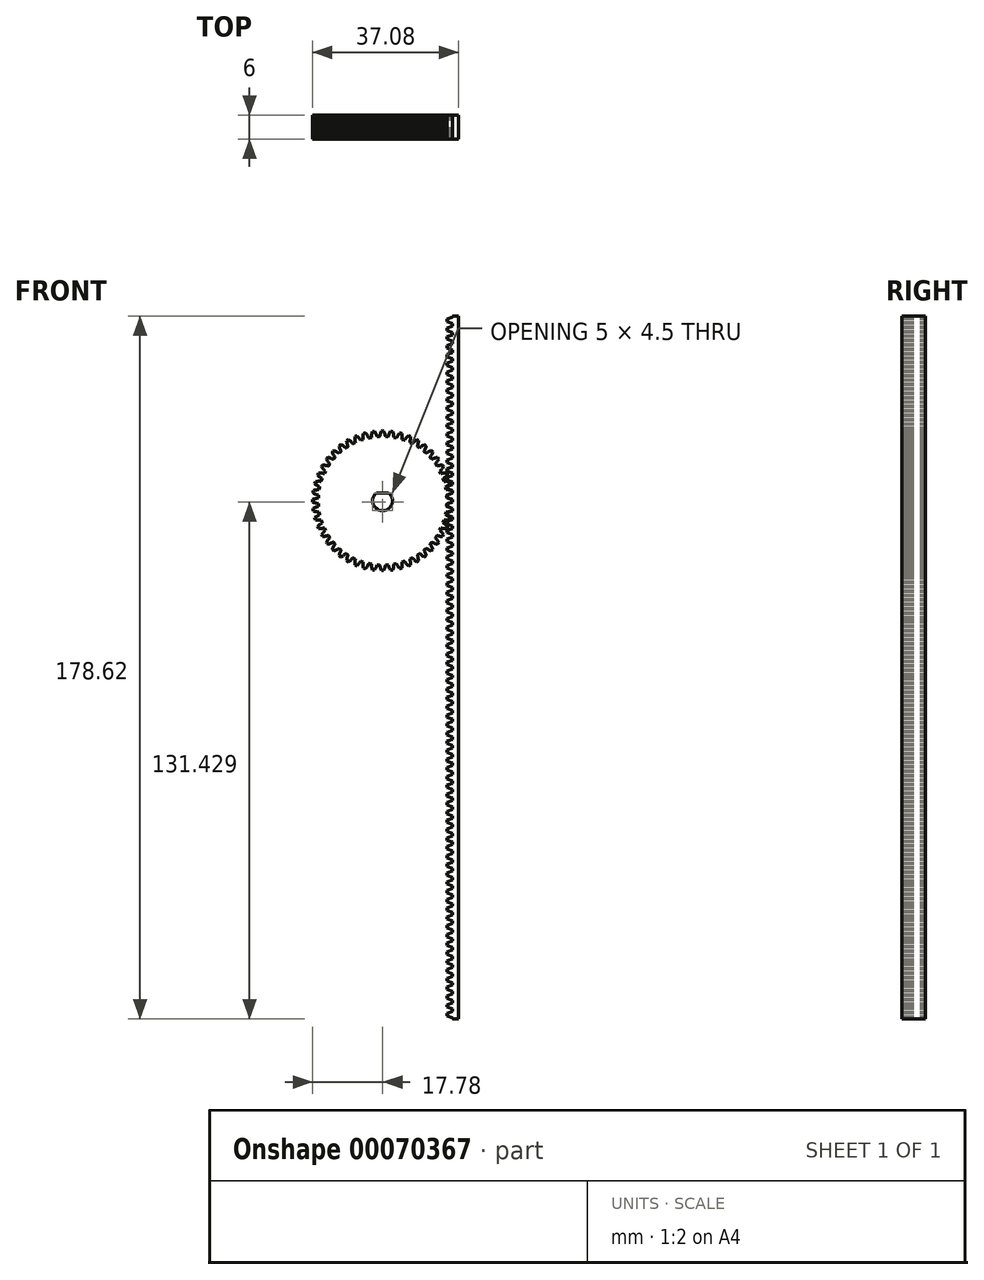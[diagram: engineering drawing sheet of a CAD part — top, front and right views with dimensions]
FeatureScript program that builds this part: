
annotation { "Feature Type Name" : "Feature", "Feature Type Description" : "" }
export const myFeature = defineFeature(function(context is Context, id is Id, definition is map)
    precondition{}
    {
        {
            var Q0;
            Q0=qCreatedBy(makeId("Front.planeOp"),FACE);
            var sketch = newSketch(context, id + "F0", { "sketchPlane" : qUnion([Q0])});
            skLineSegment(sketch, "E0", {"start": v(16.14, -3.72) * mm, "end": v(16.2, -3.44) * mm});
            skLineSegment(sketch, "E1", {"start": v(16.2, -3.44) * mm, "end": v(16.22, -3.15) * mm});
            skLineSegment(sketch, "E2", {"start": v(16.22, -3.15) * mm, "end": v(15.98, -3) * mm});
            skLineSegment(sketch, "E3", {"start": v(15.98, -3) * mm, "end": v(15.73, -2.88) * mm});
            skLineSegment(sketch, "E4", {"start": v(15.73, -2.88) * mm, "end": v(15.5, -2.77) * mm});
            skLineSegment(sketch, "E5", {"start": v(15.5, -2.77) * mm, "end": v(15.3, -2.69) * mm});
            skLineSegment(sketch, "E6", {"start": v(15.3, -2.69) * mm, "end": v(15.13, -2.62) * mm});
            skLineSegment(sketch, "E7", {"start": v(15.13, -2.62) * mm, "end": v(14.95, -2.57) * mm});
            skLineSegment(sketch, "E8", {"start": v(14.95, -2.57) * mm, "end": v(14.89, -2.54) * mm});
            skLineSegment(sketch, "E9", {"start": v(14.89, -2.54) * mm, "end": v(14.86, -2.5) * mm});
            skLineSegment(sketch, "E10", {"start": v(14.86, -2.5) * mm, "end": v(14.9, -1.87) * mm});
            skLineSegment(sketch, "E11", {"start": v(14.9, -1.87) * mm, "end": v(14.93, -1.84) * mm});
            skLineSegment(sketch, "E12", {"start": v(14.93, -1.84) * mm, "end": v(15, -1.82) * mm});
            skLineSegment(sketch, "E13", {"start": v(15, -1.82) * mm, "end": v(15.18, -1.78) * mm});
            skLineSegment(sketch, "E14", {"start": v(15.18, -1.78) * mm, "end": v(15.36, -1.74) * mm});
            skLineSegment(sketch, "E15", {"start": v(15.36, -1.74) * mm, "end": v(15.57, -1.69) * mm});
            skLineSegment(sketch, "E16", {"start": v(15.57, -1.69) * mm, "end": v(15.81, -1.61) * mm});
            skLineSegment(sketch, "E17", {"start": v(15.81, -1.61) * mm, "end": v(16.07, -1.52) * mm});
            skLineSegment(sketch, "E18", {"start": v(16.07, -1.52) * mm, "end": v(16.33, -1.4) * mm});
            skLineSegment(sketch, "E19", {"start": v(16.33, -1.4) * mm, "end": v(16.35, -1.12) * mm});
            skLineSegment(sketch, "E20", {"start": v(16.35, -1.12) * mm, "end": v(16.33, -0.83) * mm});
            skLineSegment(sketch, "E21", {"start": v(16.33, -0.83) * mm, "end": v(16.07, -0.72) * mm});
            skLineSegment(sketch, "E22", {"start": v(16.07, -0.72) * mm, "end": v(15.81, -0.62) * mm});
            skLineSegment(sketch, "E23", {"start": v(15.81, -0.62) * mm, "end": v(15.57, -0.55) * mm});
            skLineSegment(sketch, "E24", {"start": v(15.57, -0.55) * mm, "end": v(15.36, -0.5) * mm});
            skLineSegment(sketch, "E25", {"start": v(15.36, -0.5) * mm, "end": v(15.18, -0.45) * mm});
            skLineSegment(sketch, "E26", {"start": v(15.18, -0.45) * mm, "end": v(15, -0.42) * mm});
            skLineSegment(sketch, "E27", {"start": v(15, -0.42) * mm, "end": v(14.93, -0.4) * mm});
            skLineSegment(sketch, "E28", {"start": v(14.93, -0.4) * mm, "end": v(14.9, -0.37) * mm});
            skLineSegment(sketch, "E29", {"start": v(14.9, -0.37) * mm, "end": v(14.86, 0.27) * mm});
            skLineSegment(sketch, "E30", {"start": v(14.86, 0.27) * mm, "end": v(14.89, 0.3) * mm});
            skLineSegment(sketch, "E31", {"start": v(14.89, 0.3) * mm, "end": v(14.95, 0.33) * mm});
            skLineSegment(sketch, "E32", {"start": v(14.95, 0.33) * mm, "end": v(15.13, 0.39) * mm});
            skLineSegment(sketch, "E33", {"start": v(15.13, 0.39) * mm, "end": v(15.3, 0.45) * mm});
            skLineSegment(sketch, "E34", {"start": v(15.3, 0.45) * mm, "end": v(15.5, 0.54) * mm});
            skLineSegment(sketch, "E35", {"start": v(15.5, 0.54) * mm, "end": v(15.73, 0.64) * mm});
            skLineSegment(sketch, "E36", {"start": v(15.73, 0.64) * mm, "end": v(15.98, 0.77) * mm});
            skLineSegment(sketch, "E37", {"start": v(15.98, 0.77) * mm, "end": v(16.22, 0.91) * mm});
            skLineSegment(sketch, "E38", {"start": v(16.22, 0.91) * mm, "end": v(16.2, 1.2) * mm});
            skLineSegment(sketch, "E39", {"start": v(16.2, 1.2) * mm, "end": v(16.14, 1.49) * mm});
            skLineSegment(sketch, "E40", {"start": v(16.14, 1.49) * mm, "end": v(15.87, 1.56) * mm});
            skLineSegment(sketch, "E41", {"start": v(15.87, 1.56) * mm, "end": v(15.6, 1.62) * mm});
            skLineSegment(sketch, "E42", {"start": v(15.6, 1.62) * mm, "end": v(15.35, 1.67) * mm});
            skLineSegment(sketch, "E43", {"start": v(15.35, 1.67) * mm, "end": v(15.14, 1.7) * mm});
            skLineSegment(sketch, "E44", {"start": v(15.14, 1.7) * mm, "end": v(14.95, 1.71) * mm});
            skLineSegment(sketch, "E45", {"start": v(14.95, 1.71) * mm, "end": v(14.77, 1.72) * mm});
            skLineSegment(sketch, "E46", {"start": v(14.77, 1.72) * mm, "end": v(14.7, 1.74) * mm});
            skLineSegment(sketch, "E47", {"start": v(14.7, 1.74) * mm, "end": v(14.66, 1.76) * mm});
            skLineSegment(sketch, "E48", {"start": v(14.66, 1.76) * mm, "end": v(14.54, 2.38) * mm});
            skLineSegment(sketch, "E49", {"start": v(14.54, 2.38) * mm, "end": v(14.56, 2.42) * mm});
            skLineSegment(sketch, "E50", {"start": v(14.56, 2.42) * mm, "end": v(14.62, 2.46) * mm});
            skLineSegment(sketch, "E51", {"start": v(14.62, 2.46) * mm, "end": v(14.79, 2.54) * mm});
            skLineSegment(sketch, "E52", {"start": v(14.79, 2.54) * mm, "end": v(14.95, 2.62) * mm});
            skLineSegment(sketch, "E53", {"start": v(14.95, 2.62) * mm, "end": v(15.14, 2.73) * mm});
            skLineSegment(sketch, "E54", {"start": v(15.14, 2.73) * mm, "end": v(15.35, 2.87) * mm});
            skLineSegment(sketch, "E55", {"start": v(15.35, 2.87) * mm, "end": v(15.58, 3.03) * mm});
            skLineSegment(sketch, "E56", {"start": v(15.58, 3.03) * mm, "end": v(15.8, 3.2) * mm});
            skLineSegment(sketch, "E57", {"start": v(15.8, 3.2) * mm, "end": v(15.75, 3.48) * mm});
            skLineSegment(sketch, "E58", {"start": v(15.75, 3.48) * mm, "end": v(15.65, 3.76) * mm});
            skLineSegment(sketch, "E59", {"start": v(15.65, 3.76) * mm, "end": v(15.37, 3.8) * mm});
            skLineSegment(sketch, "E60", {"start": v(15.37, 3.8) * mm, "end": v(15.1, 3.82) * mm});
            skLineSegment(sketch, "E61", {"start": v(15.1, 3.82) * mm, "end": v(14.85, 3.83) * mm});
            skLineSegment(sketch, "E62", {"start": v(14.85, 3.83) * mm, "end": v(14.63, 3.83) * mm});
            skLineSegment(sketch, "E63", {"start": v(14.63, 3.83) * mm, "end": v(14.44, 3.83) * mm});
            skLineSegment(sketch, "E64", {"start": v(14.44, 3.83) * mm, "end": v(14.26, 3.81) * mm});
            skLineSegment(sketch, "E65", {"start": v(14.26, 3.81) * mm, "end": v(14.19, 3.82) * mm});
            skLineSegment(sketch, "E66", {"start": v(14.19, 3.82) * mm, "end": v(14.15, 3.84) * mm});
            skLineSegment(sketch, "E67", {"start": v(14.15, 3.84) * mm, "end": v(13.95, 4.44) * mm});
            skLineSegment(sketch, "E68", {"start": v(13.95, 4.44) * mm, "end": v(13.96, 4.48) * mm});
            skLineSegment(sketch, "E69", {"start": v(13.96, 4.48) * mm, "end": v(14.02, 4.52) * mm});
            skLineSegment(sketch, "E70", {"start": v(14.02, 4.52) * mm, "end": v(14.17, 4.62) * mm});
            skLineSegment(sketch, "E71", {"start": v(14.17, 4.62) * mm, "end": v(14.33, 4.73) * mm});
            skLineSegment(sketch, "E72", {"start": v(14.33, 4.73) * mm, "end": v(14.5, 4.86) * mm});
            skLineSegment(sketch, "E73", {"start": v(14.5, 4.86) * mm, "end": v(14.69, 5.02) * mm});
            skLineSegment(sketch, "E74", {"start": v(14.69, 5.02) * mm, "end": v(14.9, 5.21) * mm});
            skLineSegment(sketch, "E75", {"start": v(14.9, 5.21) * mm, "end": v(15.1, 5.41) * mm});
            skLineSegment(sketch, "E76", {"start": v(15.1, 5.41) * mm, "end": v(15, 5.69) * mm});
            skLineSegment(sketch, "E77", {"start": v(15, 5.69) * mm, "end": v(14.87, 5.95) * mm});
            skLineSegment(sketch, "E78", {"start": v(14.87, 5.95) * mm, "end": v(14.59, 5.95) * mm});
            skLineSegment(sketch, "E79", {"start": v(14.59, 5.95) * mm, "end": v(14.3, 5.94) * mm});
            skLineSegment(sketch, "E80", {"start": v(14.3, 5.94) * mm, "end": v(14.06, 5.92) * mm});
            skLineSegment(sketch, "E81", {"start": v(14.06, 5.92) * mm, "end": v(13.85, 5.89) * mm});
            skLineSegment(sketch, "E82", {"start": v(13.85, 5.89) * mm, "end": v(13.66, 5.86) * mm});
            skLineSegment(sketch, "E83", {"start": v(13.66, 5.86) * mm, "end": v(13.48, 5.82) * mm});
            skLineSegment(sketch, "E84", {"start": v(13.48, 5.82) * mm, "end": v(13.41, 5.81) * mm});
            skLineSegment(sketch, "E85", {"start": v(13.41, 5.81) * mm, "end": v(13.37, 5.83) * mm});
            skLineSegment(sketch, "E86", {"start": v(13.37, 5.83) * mm, "end": v(13.09, 6.4) * mm});
            skLineSegment(sketch, "E87", {"start": v(13.09, 6.4) * mm, "end": v(13.1, 6.44) * mm});
            skLineSegment(sketch, "E88", {"start": v(13.1, 6.44) * mm, "end": v(13.15, 6.5) * mm});
            skLineSegment(sketch, "E89", {"start": v(13.15, 6.5) * mm, "end": v(13.29, 6.61) * mm});
            skLineSegment(sketch, "E90", {"start": v(13.29, 6.61) * mm, "end": v(13.43, 6.74) * mm});
            skLineSegment(sketch, "E91", {"start": v(13.43, 6.74) * mm, "end": v(13.58, 6.9) * mm});
            skLineSegment(sketch, "E92", {"start": v(13.58, 6.9) * mm, "end": v(13.75, 7.07) * mm});
            skLineSegment(sketch, "E93", {"start": v(13.75, 7.07) * mm, "end": v(13.93, 7.29) * mm});
            skLineSegment(sketch, "E94", {"start": v(13.93, 7.29) * mm, "end": v(14.1, 7.51) * mm});
            skLineSegment(sketch, "E95", {"start": v(14.1, 7.51) * mm, "end": v(13.97, 7.77) * mm});
            skLineSegment(sketch, "E96", {"start": v(13.97, 7.77) * mm, "end": v(13.8, 8.02) * mm});
            skLineSegment(sketch, "E97", {"start": v(13.8, 8.02) * mm, "end": v(13.53, 7.98) * mm});
            skLineSegment(sketch, "E98", {"start": v(13.53, 7.98) * mm, "end": v(13.25, 7.93) * mm});
            skLineSegment(sketch, "E99", {"start": v(13.25, 7.93) * mm, "end": v(13.01, 7.88) * mm});
            skLineSegment(sketch, "E100", {"start": v(13.01, 7.88) * mm, "end": v(12.8, 7.82) * mm});
            skLineSegment(sketch, "E101", {"start": v(12.8, 7.82) * mm, "end": v(12.62, 7.77) * mm});
            skLineSegment(sketch, "E102", {"start": v(12.62, 7.77) * mm, "end": v(12.45, 7.7) * mm});
            skLineSegment(sketch, "E103", {"start": v(12.45, 7.7) * mm, "end": v(12.38, 7.7) * mm});
            skLineSegment(sketch, "E104", {"start": v(12.38, 7.7) * mm, "end": v(12.34, 7.7) * mm});
            skLineSegment(sketch, "E105", {"start": v(12.34, 7.7) * mm, "end": v(11.98, 8.23) * mm});
            skLineSegment(sketch, "E106", {"start": v(11.98, 8.23) * mm, "end": v(12, 8.27) * mm});
            skLineSegment(sketch, "E107", {"start": v(12, 8.27) * mm, "end": v(12.03, 8.33) * mm});
            skLineSegment(sketch, "E108", {"start": v(12.03, 8.33) * mm, "end": v(12.16, 8.47) * mm});
            skLineSegment(sketch, "E109", {"start": v(12.16, 8.47) * mm, "end": v(12.28, 8.6) * mm});
            skLineSegment(sketch, "E110", {"start": v(12.28, 8.6) * mm, "end": v(12.4, 8.78) * mm});
            skLineSegment(sketch, "E111", {"start": v(12.4, 8.78) * mm, "end": v(12.55, 8.99) * mm});
            skLineSegment(sketch, "E112", {"start": v(12.55, 8.99) * mm, "end": v(12.7, 9.22) * mm});
            skLineSegment(sketch, "E113", {"start": v(12.7, 9.22) * mm, "end": v(12.84, 9.47) * mm});
            skLineSegment(sketch, "E114", {"start": v(12.84, 9.47) * mm, "end": v(12.68, 9.7) * mm});
            skLineSegment(sketch, "E115", {"start": v(12.68, 9.7) * mm, "end": v(12.49, 9.93) * mm});
            skLineSegment(sketch, "E116", {"start": v(12.49, 9.93) * mm, "end": v(12.21, 9.85) * mm});
            skLineSegment(sketch, "E117", {"start": v(12.21, 9.85) * mm, "end": v(11.95, 9.77) * mm});
            skLineSegment(sketch, "E118", {"start": v(11.95, 9.77) * mm, "end": v(11.71, 9.69) * mm});
            skLineSegment(sketch, "E119", {"start": v(11.71, 9.69) * mm, "end": v(11.51, 9.6) * mm});
            skLineSegment(sketch, "E120", {"start": v(11.51, 9.6) * mm, "end": v(11.34, 9.52) * mm});
            skLineSegment(sketch, "E121", {"start": v(11.34, 9.52) * mm, "end": v(11.18, 9.44) * mm});
            skLineSegment(sketch, "E122", {"start": v(11.18, 9.44) * mm, "end": v(11.11, 9.42) * mm});
            skLineSegment(sketch, "E123", {"start": v(11.11, 9.42) * mm, "end": v(11.07, 9.42) * mm});
            skLineSegment(sketch, "E124", {"start": v(11.07, 9.42) * mm, "end": v(10.65, 9.9) * mm});
            skLineSegment(sketch, "E125", {"start": v(10.65, 9.9) * mm, "end": v(10.65, 9.94) * mm});
            skLineSegment(sketch, "E126", {"start": v(10.65, 9.94) * mm, "end": v(10.68, 10) * mm});
            skLineSegment(sketch, "E127", {"start": v(10.68, 10) * mm, "end": v(10.79, 10.16) * mm});
            skLineSegment(sketch, "E128", {"start": v(10.79, 10.16) * mm, "end": v(10.89, 10.31) * mm});
            skLineSegment(sketch, "E129", {"start": v(10.89, 10.31) * mm, "end": v(11, 10.5) * mm});
            skLineSegment(sketch, "E130", {"start": v(11, 10.5) * mm, "end": v(11.11, 10.72) * mm});
            skLineSegment(sketch, "E131", {"start": v(11.11, 10.72) * mm, "end": v(11.23, 10.98) * mm});
            skLineSegment(sketch, "E132", {"start": v(11.23, 10.98) * mm, "end": v(11.34, 11.24) * mm});
            skLineSegment(sketch, "E133", {"start": v(11.34, 11.24) * mm, "end": v(11.14, 11.46) * mm});
            skLineSegment(sketch, "E134", {"start": v(11.14, 11.46) * mm, "end": v(10.93, 11.65) * mm});
            skLineSegment(sketch, "E135", {"start": v(10.93, 11.65) * mm, "end": v(10.67, 11.54) * mm});
            skLineSegment(sketch, "E136", {"start": v(10.67, 11.54) * mm, "end": v(10.41, 11.42) * mm});
            skLineSegment(sketch, "E137", {"start": v(10.41, 11.42) * mm, "end": v(10.2, 11.3) * mm});
            skLineSegment(sketch, "E138", {"start": v(10.2, 11.3) * mm, "end": v(10, 11.2) * mm});
            skLineSegment(sketch, "E139", {"start": v(10, 11.2) * mm, "end": v(9.84, 11.1) * mm});
            skLineSegment(sketch, "E140", {"start": v(9.84, 11.1) * mm, "end": v(9.7, 11) * mm});
            skLineSegment(sketch, "E141", {"start": v(9.7, 11) * mm, "end": v(9.63, 10.96) * mm});
            skLineSegment(sketch, "E142", {"start": v(9.63, 10.96) * mm, "end": v(9.59, 10.96) * mm});
            skLineSegment(sketch, "E143", {"start": v(9.59, 10.96) * mm, "end": v(9.1, 11.38) * mm});
            skLineSegment(sketch, "E144", {"start": v(9.1, 11.38) * mm, "end": v(9.1, 11.42) * mm});
            skLineSegment(sketch, "E145", {"start": v(9.1, 11.42) * mm, "end": v(9.13, 11.5) * mm});
            skLineSegment(sketch, "E146", {"start": v(9.13, 11.5) * mm, "end": v(9.21, 11.65) * mm});
            skLineSegment(sketch, "E147", {"start": v(9.21, 11.65) * mm, "end": v(9.3, 11.82) * mm});
            skLineSegment(sketch, "E148", {"start": v(9.3, 11.82) * mm, "end": v(9.37, 12.03) * mm});
            skLineSegment(sketch, "E149", {"start": v(9.37, 12.03) * mm, "end": v(9.46, 12.26) * mm});
            skLineSegment(sketch, "E150", {"start": v(9.46, 12.26) * mm, "end": v(9.54, 12.53) * mm});
            skLineSegment(sketch, "E151", {"start": v(9.54, 12.53) * mm, "end": v(9.61, 12.8) * mm});
            skLineSegment(sketch, "E152", {"start": v(9.61, 12.8) * mm, "end": v(9.4, 12.99) * mm});
            skLineSegment(sketch, "E153", {"start": v(9.4, 12.99) * mm, "end": v(9.15, 13.15) * mm});
            skLineSegment(sketch, "E154", {"start": v(9.15, 13.15) * mm, "end": v(8.9, 13.01) * mm});
            skLineSegment(sketch, "E155", {"start": v(8.9, 13.01) * mm, "end": v(8.67, 12.86) * mm});
            skLineSegment(sketch, "E156", {"start": v(8.67, 12.86) * mm, "end": v(8.47, 12.72) * mm});
            skLineSegment(sketch, "E157", {"start": v(8.47, 12.72) * mm, "end": v(8.3, 12.59) * mm});
            skLineSegment(sketch, "E158", {"start": v(8.3, 12.59) * mm, "end": v(8.15, 12.47) * mm});
            skLineSegment(sketch, "E159", {"start": v(8.15, 12.47) * mm, "end": v(8.02, 12.34) * mm});
            skLineSegment(sketch, "E160", {"start": v(8.02, 12.34) * mm, "end": v(7.96, 12.3) * mm});
            skLineSegment(sketch, "E161", {"start": v(7.96, 12.3) * mm, "end": v(7.92, 12.3) * mm});
            skLineSegment(sketch, "E162", {"start": v(7.92, 12.3) * mm, "end": v(7.39, 12.65) * mm});
            skLineSegment(sketch, "E163", {"start": v(7.39, 12.65) * mm, "end": v(7.38, 12.7) * mm});
            skLineSegment(sketch, "E164", {"start": v(7.38, 12.7) * mm, "end": v(7.4, 12.76) * mm});
            skLineSegment(sketch, "E165", {"start": v(7.4, 12.76) * mm, "end": v(7.45, 12.93) * mm});
            skLineSegment(sketch, "E166", {"start": v(7.45, 12.93) * mm, "end": v(7.5, 13.11) * mm});
            skLineSegment(sketch, "E167", {"start": v(7.5, 13.11) * mm, "end": v(7.57, 13.32) * mm});
            skLineSegment(sketch, "E168", {"start": v(7.57, 13.32) * mm, "end": v(7.62, 13.57) * mm});
            skLineSegment(sketch, "E169", {"start": v(7.62, 13.57) * mm, "end": v(7.67, 13.84) * mm});
            skLineSegment(sketch, "E170", {"start": v(7.67, 13.84) * mm, "end": v(7.7, 14.12) * mm});
            skLineSegment(sketch, "E171", {"start": v(7.7, 14.12) * mm, "end": v(7.46, 14.28) * mm});
            skLineSegment(sketch, "E172", {"start": v(7.46, 14.28) * mm, "end": v(7.2, 14.41) * mm});
            skLineSegment(sketch, "E173", {"start": v(7.2, 14.41) * mm, "end": v(6.98, 14.24) * mm});
            skLineSegment(sketch, "E174", {"start": v(6.98, 14.24) * mm, "end": v(6.76, 14.06) * mm});
            skLineSegment(sketch, "E175", {"start": v(6.76, 14.06) * mm, "end": v(6.58, 13.9) * mm});
            skLineSegment(sketch, "E176", {"start": v(6.58, 13.9) * mm, "end": v(6.42, 13.74) * mm});
            skLineSegment(sketch, "E177", {"start": v(6.42, 13.74) * mm, "end": v(6.3, 13.6) * mm});
            skLineSegment(sketch, "E178", {"start": v(6.3, 13.6) * mm, "end": v(6.18, 13.46) * mm});
            skLineSegment(sketch, "E179", {"start": v(6.18, 13.46) * mm, "end": v(6.13, 13.42) * mm});
            skLineSegment(sketch, "E180", {"start": v(6.13, 13.42) * mm, "end": v(6.08, 13.4) * mm});
            skLineSegment(sketch, "E181", {"start": v(6.08, 13.4) * mm, "end": v(5.51, 13.68) * mm});
            skLineSegment(sketch, "E182", {"start": v(5.51, 13.68) * mm, "end": v(5.5, 13.72) * mm});
            skLineSegment(sketch, "E183", {"start": v(5.5, 13.72) * mm, "end": v(5.5, 13.8) * mm});
            skLineSegment(sketch, "E184", {"start": v(5.5, 13.8) * mm, "end": v(5.54, 13.97) * mm});
            skLineSegment(sketch, "E185", {"start": v(5.54, 13.97) * mm, "end": v(5.58, 14.16) * mm});
            skLineSegment(sketch, "E186", {"start": v(5.58, 14.16) * mm, "end": v(5.6, 14.37) * mm});
            skLineSegment(sketch, "E187", {"start": v(5.6, 14.37) * mm, "end": v(5.62, 14.62) * mm});
            skLineSegment(sketch, "E188", {"start": v(5.62, 14.62) * mm, "end": v(5.64, 14.9) * mm});
            skLineSegment(sketch, "E189", {"start": v(5.64, 14.9) * mm, "end": v(5.64, 15.18) * mm});
            skLineSegment(sketch, "E190", {"start": v(5.64, 15.18) * mm, "end": v(5.38, 15.31) * mm});
            skLineSegment(sketch, "E191", {"start": v(5.38, 15.31) * mm, "end": v(5.1, 15.4) * mm});
            skLineSegment(sketch, "E192", {"start": v(5.1, 15.4) * mm, "end": v(4.9, 15.2) * mm});
            skLineSegment(sketch, "E193", {"start": v(4.9, 15.2) * mm, "end": v(4.71, 15) * mm});
            skLineSegment(sketch, "E194", {"start": v(4.71, 15) * mm, "end": v(4.55, 14.81) * mm});
            skLineSegment(sketch, "E195", {"start": v(4.55, 14.81) * mm, "end": v(4.42, 14.64) * mm});
            skLineSegment(sketch, "E196", {"start": v(4.42, 14.64) * mm, "end": v(4.31, 14.48) * mm});
            skLineSegment(sketch, "E197", {"start": v(4.31, 14.48) * mm, "end": v(4.21, 14.33) * mm});
            skLineSegment(sketch, "E198", {"start": v(4.21, 14.33) * mm, "end": v(4.16, 14.28) * mm});
            skLineSegment(sketch, "E199", {"start": v(4.16, 14.28) * mm, "end": v(4.13, 14.26) * mm});
            skLineSegment(sketch, "E200", {"start": v(4.13, 14.26) * mm, "end": v(3.52, 14.46) * mm});
            skLineSegment(sketch, "E201", {"start": v(3.52, 14.46) * mm, "end": v(3.5, 14.5) * mm});
            skLineSegment(sketch, "E202", {"start": v(3.5, 14.5) * mm, "end": v(3.5, 14.57) * mm});
            skLineSegment(sketch, "E203", {"start": v(3.5, 14.57) * mm, "end": v(3.51, 14.76) * mm});
            skLineSegment(sketch, "E204", {"start": v(3.51, 14.76) * mm, "end": v(3.52, 14.94) * mm});
            skLineSegment(sketch, "E205", {"start": v(3.52, 14.94) * mm, "end": v(3.52, 15.16) * mm});
            skLineSegment(sketch, "E206", {"start": v(3.52, 15.16) * mm, "end": v(3.51, 15.4) * mm});
            skLineSegment(sketch, "E207", {"start": v(3.51, 15.4) * mm, "end": v(3.49, 15.69) * mm});
            skLineSegment(sketch, "E208", {"start": v(3.49, 15.69) * mm, "end": v(3.45, 15.96) * mm});
            skLineSegment(sketch, "E209", {"start": v(3.45, 15.96) * mm, "end": v(3.17, 16.06) * mm});
            skLineSegment(sketch, "E210", {"start": v(3.17, 16.06) * mm, "end": v(2.89, 16.11) * mm});
            skLineSegment(sketch, "E211", {"start": v(2.89, 16.11) * mm, "end": v(2.72, 15.9) * mm});
            skLineSegment(sketch, "E212", {"start": v(2.72, 15.9) * mm, "end": v(2.56, 15.66) * mm});
            skLineSegment(sketch, "E213", {"start": v(2.56, 15.66) * mm, "end": v(2.42, 15.45) * mm});
            skLineSegment(sketch, "E214", {"start": v(2.42, 15.45) * mm, "end": v(2.31, 15.27) * mm});
            skLineSegment(sketch, "E215", {"start": v(2.31, 15.27) * mm, "end": v(2.23, 15.1) * mm});
            skLineSegment(sketch, "E216", {"start": v(2.23, 15.1) * mm, "end": v(2.15, 14.93) * mm});
            skLineSegment(sketch, "E217", {"start": v(2.15, 14.93) * mm, "end": v(2.1, 14.88) * mm});
            skLineSegment(sketch, "E218", {"start": v(2.1, 14.88) * mm, "end": v(2.07, 14.85) * mm});
            skLineSegment(sketch, "E219", {"start": v(2.07, 14.85) * mm, "end": v(1.45, 14.98) * mm});
            skLineSegment(sketch, "E220", {"start": v(1.45, 14.98) * mm, "end": v(1.42, 15.01) * mm});
            skLineSegment(sketch, "E221", {"start": v(1.42, 15.01) * mm, "end": v(1.4, 15.08) * mm});
            skLineSegment(sketch, "E222", {"start": v(1.4, 15.08) * mm, "end": v(1.4, 15.26) * mm});
            skLineSegment(sketch, "E223", {"start": v(1.4, 15.26) * mm, "end": v(1.38, 15.45) * mm});
            skLineSegment(sketch, "E224", {"start": v(1.38, 15.45) * mm, "end": v(1.35, 15.67) * mm});
            skLineSegment(sketch, "E225", {"start": v(1.35, 15.67) * mm, "end": v(1.31, 15.91) * mm});
            skLineSegment(sketch, "E226", {"start": v(1.31, 15.91) * mm, "end": v(1.25, 16.18) * mm});
            skLineSegment(sketch, "E227", {"start": v(1.25, 16.18) * mm, "end": v(1.18, 16.46) * mm});
            skLineSegment(sketch, "E228", {"start": v(1.18, 16.46) * mm, "end": v(0.9, 16.51) * mm});
            skLineSegment(sketch, "E229", {"start": v(0.9, 16.51) * mm, "end": v(0.6, 16.53) * mm});
            skLineSegment(sketch, "E230", {"start": v(0.6, 16.53) * mm, "end": v(0.46, 16.29) * mm});
            skLineSegment(sketch, "E231", {"start": v(0.46, 16.29) * mm, "end": v(0.33, 16.04) * mm});
            skLineSegment(sketch, "E232", {"start": v(0.33, 16.04) * mm, "end": v(0.23, 15.82) * mm});
            skLineSegment(sketch, "E233", {"start": v(0.23, 15.82) * mm, "end": v(0.14, 15.61) * mm});
            skLineSegment(sketch, "E234", {"start": v(0.14, 15.61) * mm, "end": v(0.08, 15.44) * mm});
            skLineSegment(sketch, "E235", {"start": v(0.08, 15.44) * mm, "end": v(0.02, 15.26) * mm});
            skLineSegment(sketch, "E236", {"start": v(0.02, 15.26) * mm, "end": v(-0.01, 15.2) * mm});
            skLineSegment(sketch, "E237", {"start": v(-0.01, 15.2) * mm, "end": v(-0.04, 15.17) * mm});
            skLineSegment(sketch, "E238", {"start": v(-0.04, 15.17) * mm, "end": v(-0.68, 15.21) * mm});
            skLineSegment(sketch, "E239", {"start": v(-0.68, 15.21) * mm, "end": v(-0.7, 15.25) * mm});
            skLineSegment(sketch, "E240", {"start": v(-0.7, 15.25) * mm, "end": v(-0.73, 15.31) * mm});
            skLineSegment(sketch, "E241", {"start": v(-0.73, 15.31) * mm, "end": v(-0.76, 15.5) * mm});
            skLineSegment(sketch, "E242", {"start": v(-0.76, 15.5) * mm, "end": v(-0.8, 15.68) * mm});
            skLineSegment(sketch, "E243", {"start": v(-0.8, 15.68) * mm, "end": v(-0.86, 15.89) * mm});
            skLineSegment(sketch, "E244", {"start": v(-0.86, 15.89) * mm, "end": v(-0.94, 16.12) * mm});
            skLineSegment(sketch, "E245", {"start": v(-0.94, 16.12) * mm, "end": v(-1.03, 16.39) * mm});
            skLineSegment(sketch, "E246", {"start": v(-1.03, 16.39) * mm, "end": v(-1.14, 16.65) * mm});
            skLineSegment(sketch, "E247", {"start": v(-1.14, 16.65) * mm, "end": v(-1.43, 16.66) * mm});
            skLineSegment(sketch, "E248", {"start": v(-1.43, 16.66) * mm, "end": v(-1.72, 16.65) * mm});
            skLineSegment(sketch, "E249", {"start": v(-1.72, 16.65) * mm, "end": v(-1.83, 16.39) * mm});
            skLineSegment(sketch, "E250", {"start": v(-1.83, 16.39) * mm, "end": v(-1.92, 16.12) * mm});
            skLineSegment(sketch, "E251", {"start": v(-1.92, 16.12) * mm, "end": v(-2, 15.89) * mm});
            skLineSegment(sketch, "E252", {"start": v(-2, 15.89) * mm, "end": v(-2.06, 15.68) * mm});
            skLineSegment(sketch, "E253", {"start": v(-2.06, 15.68) * mm, "end": v(-2.1, 15.5) * mm});
            skLineSegment(sketch, "E254", {"start": v(-2.1, 15.5) * mm, "end": v(-2.13, 15.31) * mm});
            skLineSegment(sketch, "E255", {"start": v(-2.13, 15.31) * mm, "end": v(-2.15, 15.25) * mm});
            skLineSegment(sketch, "E256", {"start": v(-2.15, 15.25) * mm, "end": v(-2.18, 15.21) * mm});
            skLineSegment(sketch, "E257", {"start": v(-2.18, 15.21) * mm, "end": v(-2.82, 15.17) * mm});
            skLineSegment(sketch, "E258", {"start": v(-2.82, 15.17) * mm, "end": v(-2.85, 15.2) * mm});
            skLineSegment(sketch, "E259", {"start": v(-2.85, 15.2) * mm, "end": v(-2.88, 15.26) * mm});
            skLineSegment(sketch, "E260", {"start": v(-2.88, 15.26) * mm, "end": v(-2.94, 15.44) * mm});
            skLineSegment(sketch, "E261", {"start": v(-2.94, 15.44) * mm, "end": v(-3, 15.61) * mm});
            skLineSegment(sketch, "E262", {"start": v(-3, 15.61) * mm, "end": v(-3.08, 15.82) * mm});
            skLineSegment(sketch, "E263", {"start": v(-3.08, 15.82) * mm, "end": v(-3.19, 16.04) * mm});
            skLineSegment(sketch, "E264", {"start": v(-3.19, 16.04) * mm, "end": v(-3.32, 16.29) * mm});
            skLineSegment(sketch, "E265", {"start": v(-3.32, 16.29) * mm, "end": v(-3.46, 16.53) * mm});
            skLineSegment(sketch, "E266", {"start": v(-3.46, 16.53) * mm, "end": v(-3.75, 16.51) * mm});
            skLineSegment(sketch, "E267", {"start": v(-3.75, 16.51) * mm, "end": v(-4.04, 16.46) * mm});
            skLineSegment(sketch, "E268", {"start": v(-4.04, 16.46) * mm, "end": v(-4.1, 16.18) * mm});
            skLineSegment(sketch, "E269", {"start": v(-4.1, 16.18) * mm, "end": v(-4.17, 15.91) * mm});
            skLineSegment(sketch, "E270", {"start": v(-4.17, 15.91) * mm, "end": v(-4.21, 15.67) * mm});
            skLineSegment(sketch, "E271", {"start": v(-4.21, 15.67) * mm, "end": v(-4.24, 15.45) * mm});
            skLineSegment(sketch, "E272", {"start": v(-4.24, 15.45) * mm, "end": v(-4.26, 15.26) * mm});
            skLineSegment(sketch, "E273", {"start": v(-4.26, 15.26) * mm, "end": v(-4.27, 15.08) * mm});
            skLineSegment(sketch, "E274", {"start": v(-4.27, 15.08) * mm, "end": v(-4.28, 15.01) * mm});
            skLineSegment(sketch, "E275", {"start": v(-4.28, 15.01) * mm, "end": v(-4.3, 14.98) * mm});
            skLineSegment(sketch, "E276", {"start": v(-4.3, 14.98) * mm, "end": v(-4.93, 14.85) * mm});
            skLineSegment(sketch, "E277", {"start": v(-4.93, 14.85) * mm, "end": v(-4.97, 14.88) * mm});
            skLineSegment(sketch, "E278", {"start": v(-4.97, 14.88) * mm, "end": v(-5, 14.93) * mm});
            skLineSegment(sketch, "E279", {"start": v(-5, 14.93) * mm, "end": v(-5.08, 15.1) * mm});
            skLineSegment(sketch, "E280", {"start": v(-5.08, 15.1) * mm, "end": v(-5.17, 15.27) * mm});
            skLineSegment(sketch, "E281", {"start": v(-5.17, 15.27) * mm, "end": v(-5.28, 15.45) * mm});
            skLineSegment(sketch, "E282", {"start": v(-5.28, 15.45) * mm, "end": v(-5.41, 15.66) * mm});
            skLineSegment(sketch, "E283", {"start": v(-5.41, 15.66) * mm, "end": v(-5.57, 15.9) * mm});
            skLineSegment(sketch, "E284", {"start": v(-5.57, 15.9) * mm, "end": v(-5.75, 16.11) * mm});
            skLineSegment(sketch, "E285", {"start": v(-5.75, 16.11) * mm, "end": v(-6.03, 16.06) * mm});
            skLineSegment(sketch, "E286", {"start": v(-6.03, 16.06) * mm, "end": v(-6.3, 15.96) * mm});
            skLineSegment(sketch, "E287", {"start": v(-6.3, 15.96) * mm, "end": v(-6.34, 15.69) * mm});
            skLineSegment(sketch, "E288", {"start": v(-6.34, 15.69) * mm, "end": v(-6.37, 15.4) * mm});
            skLineSegment(sketch, "E289", {"start": v(-6.37, 15.4) * mm, "end": v(-6.38, 15.16) * mm});
            skLineSegment(sketch, "E290", {"start": v(-6.38, 15.16) * mm, "end": v(-6.38, 14.94) * mm});
            skLineSegment(sketch, "E291", {"start": v(-6.38, 14.94) * mm, "end": v(-6.37, 14.76) * mm});
            skLineSegment(sketch, "E292", {"start": v(-6.37, 14.76) * mm, "end": v(-6.36, 14.57) * mm});
            skLineSegment(sketch, "E293", {"start": v(-6.36, 14.57) * mm, "end": v(-6.36, 14.5) * mm});
            skLineSegment(sketch, "E294", {"start": v(-6.36, 14.5) * mm, "end": v(-6.38, 14.46) * mm});
            skLineSegment(sketch, "E295", {"start": v(-6.38, 14.46) * mm, "end": v(-6.98, 14.26) * mm});
            skLineSegment(sketch, "E296", {"start": v(-6.98, 14.26) * mm, "end": v(-7.02, 14.28) * mm});
            skLineSegment(sketch, "E297", {"start": v(-7.02, 14.28) * mm, "end": v(-7.07, 14.33) * mm});
            skLineSegment(sketch, "E298", {"start": v(-7.07, 14.33) * mm, "end": v(-7.17, 14.48) * mm});
            skLineSegment(sketch, "E299", {"start": v(-7.17, 14.48) * mm, "end": v(-7.28, 14.64) * mm});
            skLineSegment(sketch, "E300", {"start": v(-7.28, 14.64) * mm, "end": v(-7.41, 14.81) * mm});
            skLineSegment(sketch, "E301", {"start": v(-7.41, 14.81) * mm, "end": v(-7.57, 15) * mm});
            skLineSegment(sketch, "E302", {"start": v(-7.57, 15) * mm, "end": v(-7.76, 15.2) * mm});
            skLineSegment(sketch, "E303", {"start": v(-7.76, 15.2) * mm, "end": v(-7.96, 15.4) * mm});
            skLineSegment(sketch, "E304", {"start": v(-7.96, 15.4) * mm, "end": v(-8.23, 15.31) * mm});
            skLineSegment(sketch, "E305", {"start": v(-8.23, 15.31) * mm, "end": v(-8.5, 15.18) * mm});
            skLineSegment(sketch, "E306", {"start": v(-8.5, 15.18) * mm, "end": v(-8.5, 14.9) * mm});
            skLineSegment(sketch, "E307", {"start": v(-8.5, 14.9) * mm, "end": v(-8.48, 14.62) * mm});
            skLineSegment(sketch, "E308", {"start": v(-8.48, 14.62) * mm, "end": v(-8.46, 14.37) * mm});
            skLineSegment(sketch, "E309", {"start": v(-8.46, 14.37) * mm, "end": v(-8.43, 14.16) * mm});
            skLineSegment(sketch, "E310", {"start": v(-8.43, 14.16) * mm, "end": v(-8.4, 13.97) * mm});
            skLineSegment(sketch, "E311", {"start": v(-8.4, 13.97) * mm, "end": v(-8.36, 13.8) * mm});
            skLineSegment(sketch, "E312", {"start": v(-8.36, 13.8) * mm, "end": v(-8.36, 13.72) * mm});
            skLineSegment(sketch, "E313", {"start": v(-8.36, 13.72) * mm, "end": v(-8.37, 13.68) * mm});
            skLineSegment(sketch, "E314", {"start": v(-8.37, 13.68) * mm, "end": v(-8.94, 13.4) * mm});
            skLineSegment(sketch, "E315", {"start": v(-8.94, 13.4) * mm, "end": v(-8.99, 13.42) * mm});
            skLineSegment(sketch, "E316", {"start": v(-8.99, 13.42) * mm, "end": v(-9.04, 13.46) * mm});
            skLineSegment(sketch, "E317", {"start": v(-9.04, 13.46) * mm, "end": v(-9.16, 13.6) * mm});
            skLineSegment(sketch, "E318", {"start": v(-9.16, 13.6) * mm, "end": v(-9.28, 13.74) * mm});
            skLineSegment(sketch, "E319", {"start": v(-9.28, 13.74) * mm, "end": v(-9.44, 13.9) * mm});
            skLineSegment(sketch, "E320", {"start": v(-9.44, 13.9) * mm, "end": v(-9.62, 14.06) * mm});
            skLineSegment(sketch, "E321", {"start": v(-9.62, 14.06) * mm, "end": v(-9.84, 14.24) * mm});
            skLineSegment(sketch, "E322", {"start": v(-9.84, 14.24) * mm, "end": v(-10.06, 14.41) * mm});
            skLineSegment(sketch, "E323", {"start": v(-10.06, 14.41) * mm, "end": v(-10.32, 14.28) * mm});
            skLineSegment(sketch, "E324", {"start": v(-10.32, 14.28) * mm, "end": v(-10.56, 14.12) * mm});
            skLineSegment(sketch, "E325", {"start": v(-10.56, 14.12) * mm, "end": v(-10.53, 13.84) * mm});
            skLineSegment(sketch, "E326", {"start": v(-10.53, 13.84) * mm, "end": v(-10.48, 13.57) * mm});
            skLineSegment(sketch, "E327", {"start": v(-10.48, 13.57) * mm, "end": v(-10.42, 13.32) * mm});
            skLineSegment(sketch, "E328", {"start": v(-10.42, 13.32) * mm, "end": v(-10.37, 13.11) * mm});
            skLineSegment(sketch, "E329", {"start": v(-10.37, 13.11) * mm, "end": v(-10.31, 12.93) * mm});
            skLineSegment(sketch, "E330", {"start": v(-10.31, 12.93) * mm, "end": v(-10.25, 12.76) * mm});
            skLineSegment(sketch, "E331", {"start": v(-10.25, 12.76) * mm, "end": v(-10.24, 12.7) * mm});
            skLineSegment(sketch, "E332", {"start": v(-10.24, 12.7) * mm, "end": v(-10.25, 12.65) * mm});
            skLineSegment(sketch, "E333", {"start": v(-10.25, 12.65) * mm, "end": v(-10.77, 12.3) * mm});
            skLineSegment(sketch, "E334", {"start": v(-10.77, 12.3) * mm, "end": v(-10.82, 12.3) * mm});
            skLineSegment(sketch, "E335", {"start": v(-10.82, 12.3) * mm, "end": v(-10.88, 12.34) * mm});
            skLineSegment(sketch, "E336", {"start": v(-10.88, 12.34) * mm, "end": v(-11.01, 12.47) * mm});
            skLineSegment(sketch, "E337", {"start": v(-11.01, 12.47) * mm, "end": v(-11.16, 12.59) * mm});
            skLineSegment(sketch, "E338", {"start": v(-11.16, 12.59) * mm, "end": v(-11.33, 12.72) * mm});
            skLineSegment(sketch, "E339", {"start": v(-11.33, 12.72) * mm, "end": v(-11.53, 12.86) * mm});
            skLineSegment(sketch, "E340", {"start": v(-11.53, 12.86) * mm, "end": v(-11.77, 13.01) * mm});
            skLineSegment(sketch, "E341", {"start": v(-11.77, 13.01) * mm, "end": v(-12.01, 13.15) * mm});
            skLineSegment(sketch, "E342", {"start": v(-12.01, 13.15) * mm, "end": v(-12.25, 12.99) * mm});
            skLineSegment(sketch, "E343", {"start": v(-12.25, 12.99) * mm, "end": v(-12.47, 12.8) * mm});
            skLineSegment(sketch, "E344", {"start": v(-12.47, 12.8) * mm, "end": v(-12.4, 12.53) * mm});
            skLineSegment(sketch, "E345", {"start": v(-12.4, 12.53) * mm, "end": v(-12.32, 12.26) * mm});
            skLineSegment(sketch, "E346", {"start": v(-12.32, 12.26) * mm, "end": v(-12.23, 12.03) * mm});
            skLineSegment(sketch, "E347", {"start": v(-12.23, 12.03) * mm, "end": v(-12.15, 11.82) * mm});
            skLineSegment(sketch, "E348", {"start": v(-12.15, 11.82) * mm, "end": v(-12.07, 11.65) * mm});
            skLineSegment(sketch, "E349", {"start": v(-12.07, 11.65) * mm, "end": v(-11.99, 11.5) * mm});
            skLineSegment(sketch, "E350", {"start": v(-11.99, 11.5) * mm, "end": v(-11.96, 11.42) * mm});
            skLineSegment(sketch, "E351", {"start": v(-11.96, 11.42) * mm, "end": v(-11.97, 11.38) * mm});
            skLineSegment(sketch, "E352", {"start": v(-11.97, 11.38) * mm, "end": v(-12.45, 10.96) * mm});
            skLineSegment(sketch, "E353", {"start": v(-12.45, 10.96) * mm, "end": v(-12.49, 10.96) * mm});
            skLineSegment(sketch, "E354", {"start": v(-12.49, 10.96) * mm, "end": v(-12.55, 11) * mm});
            skLineSegment(sketch, "E355", {"start": v(-12.55, 11) * mm, "end": v(-12.7, 11.1) * mm});
            skLineSegment(sketch, "E356", {"start": v(-12.7, 11.1) * mm, "end": v(-12.86, 11.2) * mm});
            skLineSegment(sketch, "E357", {"start": v(-12.86, 11.2) * mm, "end": v(-13.05, 11.3) * mm});
            skLineSegment(sketch, "E358", {"start": v(-13.05, 11.3) * mm, "end": v(-13.27, 11.42) * mm});
            skLineSegment(sketch, "E359", {"start": v(-13.27, 11.42) * mm, "end": v(-13.52, 11.54) * mm});
            skLineSegment(sketch, "E360", {"start": v(-13.52, 11.54) * mm, "end": v(-13.78, 11.65) * mm});
            skLineSegment(sketch, "E361", {"start": v(-13.78, 11.65) * mm, "end": v(-14, 11.46) * mm});
            skLineSegment(sketch, "E362", {"start": v(-14, 11.46) * mm, "end": v(-14.2, 11.24) * mm});
            skLineSegment(sketch, "E363", {"start": v(-14.2, 11.24) * mm, "end": v(-14.09, 10.98) * mm});
            skLineSegment(sketch, "E364", {"start": v(-14.09, 10.98) * mm, "end": v(-13.97, 10.72) * mm});
            skLineSegment(sketch, "E365", {"start": v(-13.97, 10.72) * mm, "end": v(-13.86, 10.5) * mm});
            skLineSegment(sketch, "E366", {"start": v(-13.86, 10.5) * mm, "end": v(-13.75, 10.31) * mm});
            skLineSegment(sketch, "E367", {"start": v(-13.75, 10.31) * mm, "end": v(-13.65, 10.16) * mm});
            skLineSegment(sketch, "E368", {"start": v(-13.65, 10.16) * mm, "end": v(-13.54, 10) * mm});
            skLineSegment(sketch, "E369", {"start": v(-13.54, 10) * mm, "end": v(-13.51, 9.94) * mm});
            skLineSegment(sketch, "E370", {"start": v(-13.51, 9.94) * mm, "end": v(-13.5, 9.9) * mm});
            skLineSegment(sketch, "E371", {"start": v(-13.5, 9.9) * mm, "end": v(-13.93, 9.42) * mm});
            skLineSegment(sketch, "E372", {"start": v(-13.93, 9.42) * mm, "end": v(-13.97, 9.42) * mm});
            skLineSegment(sketch, "E373", {"start": v(-13.97, 9.42) * mm, "end": v(-14.04, 9.44) * mm});
            skLineSegment(sketch, "E374", {"start": v(-14.04, 9.44) * mm, "end": v(-14.2, 9.52) * mm});
            skLineSegment(sketch, "E375", {"start": v(-14.2, 9.52) * mm, "end": v(-14.37, 9.6) * mm});
            skLineSegment(sketch, "E376", {"start": v(-14.37, 9.6) * mm, "end": v(-14.57, 9.69) * mm});
            skLineSegment(sketch, "E377", {"start": v(-14.57, 9.69) * mm, "end": v(-14.8, 9.77) * mm});
            skLineSegment(sketch, "E378", {"start": v(-14.8, 9.77) * mm, "end": v(-15.07, 9.85) * mm});
            skLineSegment(sketch, "E379", {"start": v(-15.07, 9.85) * mm, "end": v(-15.34, 9.93) * mm});
            skLineSegment(sketch, "E380", {"start": v(-15.34, 9.93) * mm, "end": v(-15.54, 9.7) * mm});
            skLineSegment(sketch, "E381", {"start": v(-15.54, 9.7) * mm, "end": v(-15.7, 9.47) * mm});
            skLineSegment(sketch, "E382", {"start": v(-15.7, 9.47) * mm, "end": v(-15.56, 9.22) * mm});
            skLineSegment(sketch, "E383", {"start": v(-15.56, 9.22) * mm, "end": v(-15.4, 8.99) * mm});
            skLineSegment(sketch, "E384", {"start": v(-15.4, 8.99) * mm, "end": v(-15.27, 8.78) * mm});
            skLineSegment(sketch, "E385", {"start": v(-15.27, 8.78) * mm, "end": v(-15.13, 8.6) * mm});
            skLineSegment(sketch, "E386", {"start": v(-15.13, 8.6) * mm, "end": v(-15.01, 8.47) * mm});
            skLineSegment(sketch, "E387", {"start": v(-15.01, 8.47) * mm, "end": v(-14.89, 8.33) * mm});
            skLineSegment(sketch, "E388", {"start": v(-14.89, 8.33) * mm, "end": v(-14.85, 8.27) * mm});
            skLineSegment(sketch, "E389", {"start": v(-14.85, 8.27) * mm, "end": v(-14.84, 8.23) * mm});
            skLineSegment(sketch, "E390", {"start": v(-14.84, 8.23) * mm, "end": v(-15.2, 7.7) * mm});
            skLineSegment(sketch, "E391", {"start": v(-15.2, 7.7) * mm, "end": v(-15.24, 7.7) * mm});
            skLineSegment(sketch, "E392", {"start": v(-15.24, 7.7) * mm, "end": v(-15.3, 7.7) * mm});
            skLineSegment(sketch, "E393", {"start": v(-15.3, 7.7) * mm, "end": v(-15.48, 7.77) * mm});
            skLineSegment(sketch, "E394", {"start": v(-15.48, 7.77) * mm, "end": v(-15.66, 7.82) * mm});
            skLineSegment(sketch, "E395", {"start": v(-15.66, 7.82) * mm, "end": v(-15.87, 7.88) * mm});
            skLineSegment(sketch, "E396", {"start": v(-15.87, 7.88) * mm, "end": v(-16.11, 7.93) * mm});
            skLineSegment(sketch, "E397", {"start": v(-16.11, 7.93) * mm, "end": v(-16.39, 7.98) * mm});
            skLineSegment(sketch, "E398", {"start": v(-16.39, 7.98) * mm, "end": v(-16.67, 8.02) * mm});
            skLineSegment(sketch, "E399", {"start": v(-16.67, 8.02) * mm, "end": v(-16.83, 7.77) * mm});
            skLineSegment(sketch, "E400", {"start": v(-16.83, 7.77) * mm, "end": v(-16.96, 7.51) * mm});
            skLineSegment(sketch, "E401", {"start": v(-16.96, 7.51) * mm, "end": v(-16.79, 7.29) * mm});
            skLineSegment(sketch, "E402", {"start": v(-16.79, 7.29) * mm, "end": v(-16.6, 7.07) * mm});
            skLineSegment(sketch, "E403", {"start": v(-16.6, 7.07) * mm, "end": v(-16.44, 6.9) * mm});
            skLineSegment(sketch, "E404", {"start": v(-16.44, 6.9) * mm, "end": v(-16.29, 6.74) * mm});
            skLineSegment(sketch, "E405", {"start": v(-16.29, 6.74) * mm, "end": v(-16.15, 6.61) * mm});
            skLineSegment(sketch, "E406", {"start": v(-16.15, 6.61) * mm, "end": v(-16, 6.5) * mm});
            skLineSegment(sketch, "E407", {"start": v(-16, 6.5) * mm, "end": v(-15.96, 6.44) * mm});
            skLineSegment(sketch, "E408", {"start": v(-15.96, 6.44) * mm, "end": v(-15.95, 6.4) * mm});
            skLineSegment(sketch, "E409", {"start": v(-15.95, 6.4) * mm, "end": v(-16.23, 5.83) * mm});
            skLineSegment(sketch, "E410", {"start": v(-16.23, 5.83) * mm, "end": v(-16.27, 5.81) * mm});
            skLineSegment(sketch, "E411", {"start": v(-16.27, 5.81) * mm, "end": v(-16.34, 5.82) * mm});
            skLineSegment(sketch, "E412", {"start": v(-16.34, 5.82) * mm, "end": v(-16.52, 5.86) * mm});
            skLineSegment(sketch, "E413", {"start": v(-16.52, 5.86) * mm, "end": v(-16.7, 5.89) * mm});
            skLineSegment(sketch, "E414", {"start": v(-16.7, 5.89) * mm, "end": v(-16.92, 5.92) * mm});
            skLineSegment(sketch, "E415", {"start": v(-16.92, 5.92) * mm, "end": v(-17.17, 5.94) * mm});
            skLineSegment(sketch, "E416", {"start": v(-17.17, 5.94) * mm, "end": v(-17.45, 5.95) * mm});
            skLineSegment(sketch, "E417", {"start": v(-17.45, 5.95) * mm, "end": v(-17.73, 5.95) * mm});
            skLineSegment(sketch, "E418", {"start": v(-17.73, 5.95) * mm, "end": v(-17.86, 5.69) * mm});
            skLineSegment(sketch, "E419", {"start": v(-17.86, 5.69) * mm, "end": v(-17.95, 5.41) * mm});
            skLineSegment(sketch, "E420", {"start": v(-17.95, 5.41) * mm, "end": v(-17.75, 5.21) * mm});
            skLineSegment(sketch, "E421", {"start": v(-17.75, 5.21) * mm, "end": v(-17.55, 5.02) * mm});
            skLineSegment(sketch, "E422", {"start": v(-17.55, 5.02) * mm, "end": v(-17.36, 4.86) * mm});
            skLineSegment(sketch, "E423", {"start": v(-17.36, 4.86) * mm, "end": v(-17.18, 4.73) * mm});
            skLineSegment(sketch, "E424", {"start": v(-17.18, 4.73) * mm, "end": v(-17.03, 4.62) * mm});
            skLineSegment(sketch, "E425", {"start": v(-17.03, 4.62) * mm, "end": v(-16.88, 4.52) * mm});
            skLineSegment(sketch, "E426", {"start": v(-16.88, 4.52) * mm, "end": v(-16.82, 4.48) * mm});
            skLineSegment(sketch, "E427", {"start": v(-16.82, 4.48) * mm, "end": v(-16.8, 4.44) * mm});
            skLineSegment(sketch, "E428", {"start": v(-16.8, 4.44) * mm, "end": v(-17, 3.84) * mm});
            skLineSegment(sketch, "E429", {"start": v(-17, 3.84) * mm, "end": v(-17.05, 3.82) * mm});
            skLineSegment(sketch, "E430", {"start": v(-17.05, 3.82) * mm, "end": v(-17.12, 3.81) * mm});
            skLineSegment(sketch, "E431", {"start": v(-17.12, 3.81) * mm, "end": v(-17.3, 3.83) * mm});
            skLineSegment(sketch, "E432", {"start": v(-17.3, 3.83) * mm, "end": v(-17.49, 3.83) * mm});
            skLineSegment(sketch, "E433", {"start": v(-17.49, 3.83) * mm, "end": v(-17.7, 3.83) * mm});
            skLineSegment(sketch, "E434", {"start": v(-17.7, 3.83) * mm, "end": v(-17.95, 3.82) * mm});
            skLineSegment(sketch, "E435", {"start": v(-17.95, 3.82) * mm, "end": v(-18.23, 3.8) * mm});
            skLineSegment(sketch, "E436", {"start": v(-18.23, 3.8) * mm, "end": v(-18.51, 3.76) * mm});
            skLineSegment(sketch, "E437", {"start": v(-18.51, 3.76) * mm, "end": v(-18.6, 3.48) * mm});
            skLineSegment(sketch, "E438", {"start": v(-18.6, 3.48) * mm, "end": v(-18.66, 3.2) * mm});
            skLineSegment(sketch, "E439", {"start": v(-18.66, 3.2) * mm, "end": v(-18.44, 3.03) * mm});
            skLineSegment(sketch, "E440", {"start": v(-18.44, 3.03) * mm, "end": v(-18.21, 2.87) * mm});
            skLineSegment(sketch, "E441", {"start": v(-18.21, 2.87) * mm, "end": v(-18, 2.73) * mm});
            skLineSegment(sketch, "E442", {"start": v(-18, 2.73) * mm, "end": v(-17.81, 2.62) * mm});
            skLineSegment(sketch, "E443", {"start": v(-17.81, 2.62) * mm, "end": v(-17.65, 2.54) * mm});
            skLineSegment(sketch, "E444", {"start": v(-17.65, 2.54) * mm, "end": v(-17.48, 2.46) * mm});
            skLineSegment(sketch, "E445", {"start": v(-17.48, 2.46) * mm, "end": v(-17.42, 2.42) * mm});
            skLineSegment(sketch, "E446", {"start": v(-17.42, 2.42) * mm, "end": v(-17.4, 2.38) * mm});
            skLineSegment(sketch, "E447", {"start": v(-17.4, 2.38) * mm, "end": v(-17.52, 1.76) * mm});
            skLineSegment(sketch, "E448", {"start": v(-17.52, 1.76) * mm, "end": v(-17.56, 1.74) * mm});
            skLineSegment(sketch, "E449", {"start": v(-17.56, 1.74) * mm, "end": v(-17.63, 1.72) * mm});
            skLineSegment(sketch, "E450", {"start": v(-17.63, 1.72) * mm, "end": v(-17.81, 1.71) * mm});
            skLineSegment(sketch, "E451", {"start": v(-17.81, 1.71) * mm, "end": v(-18, 1.7) * mm});
            skLineSegment(sketch, "E452", {"start": v(-18, 1.7) * mm, "end": v(-18.21, 1.67) * mm});
            skLineSegment(sketch, "E453", {"start": v(-18.21, 1.67) * mm, "end": v(-18.46, 1.62) * mm});
            skLineSegment(sketch, "E454", {"start": v(-18.46, 1.62) * mm, "end": v(-18.73, 1.56) * mm});
            skLineSegment(sketch, "E455", {"start": v(-18.73, 1.56) * mm, "end": v(-19, 1.49) * mm});
            skLineSegment(sketch, "E456", {"start": v(-19, 1.49) * mm, "end": v(-19.06, 1.2) * mm});
            skLineSegment(sketch, "E457", {"start": v(-19.06, 1.2) * mm, "end": v(-19.08, 0.91) * mm});
            skLineSegment(sketch, "E458", {"start": v(-19.08, 0.91) * mm, "end": v(-18.83, 0.77) * mm});
            skLineSegment(sketch, "E459", {"start": v(-18.83, 0.77) * mm, "end": v(-18.59, 0.64) * mm});
            skLineSegment(sketch, "E460", {"start": v(-18.59, 0.64) * mm, "end": v(-18.36, 0.54) * mm});
            skLineSegment(sketch, "E461", {"start": v(-18.36, 0.54) * mm, "end": v(-18.16, 0.45) * mm});
            skLineSegment(sketch, "E462", {"start": v(-18.16, 0.45) * mm, "end": v(-17.99, 0.39) * mm});
            skLineSegment(sketch, "E463", {"start": v(-17.99, 0.39) * mm, "end": v(-17.8, 0.33) * mm});
            skLineSegment(sketch, "E464", {"start": v(-17.8, 0.33) * mm, "end": v(-17.75, 0.3) * mm});
            skLineSegment(sketch, "E465", {"start": v(-17.75, 0.3) * mm, "end": v(-17.72, 0.27) * mm});
            skLineSegment(sketch, "E466", {"start": v(-17.72, 0.27) * mm, "end": v(-17.76, -0.37) * mm});
            skLineSegment(sketch, "E467", {"start": v(-17.76, -0.37) * mm, "end": v(-17.8, -0.4) * mm});
            skLineSegment(sketch, "E468", {"start": v(-17.8, -0.4) * mm, "end": v(-17.86, -0.42) * mm});
            skLineSegment(sketch, "E469", {"start": v(-17.86, -0.42) * mm, "end": v(-18.04, -0.45) * mm});
            skLineSegment(sketch, "E470", {"start": v(-18.04, -0.45) * mm, "end": v(-18.22, -0.5) * mm});
            skLineSegment(sketch, "E471", {"start": v(-18.22, -0.5) * mm, "end": v(-18.43, -0.55) * mm});
            skLineSegment(sketch, "E472", {"start": v(-18.43, -0.55) * mm, "end": v(-18.67, -0.62) * mm});
            skLineSegment(sketch, "E473", {"start": v(-18.67, -0.62) * mm, "end": v(-18.93, -0.72) * mm});
            skLineSegment(sketch, "E474", {"start": v(-18.93, -0.72) * mm, "end": v(-19.2, -0.83) * mm});
            skLineSegment(sketch, "E475", {"start": v(-19.2, -0.83) * mm, "end": v(-19.21, -1.12) * mm});
            skLineSegment(sketch, "E476", {"start": v(-19.21, -1.12) * mm, "end": v(-19.2, -1.4) * mm});
            skLineSegment(sketch, "E477", {"start": v(-19.2, -1.4) * mm, "end": v(-18.93, -1.52) * mm});
            skLineSegment(sketch, "E478", {"start": v(-18.93, -1.52) * mm, "end": v(-18.67, -1.61) * mm});
            skLineSegment(sketch, "E479", {"start": v(-18.67, -1.61) * mm, "end": v(-18.43, -1.69) * mm});
            skLineSegment(sketch, "E480", {"start": v(-18.43, -1.69) * mm, "end": v(-18.22, -1.74) * mm});
            skLineSegment(sketch, "E481", {"start": v(-18.22, -1.74) * mm, "end": v(-18.04, -1.78) * mm});
            skLineSegment(sketch, "E482", {"start": v(-18.04, -1.78) * mm, "end": v(-17.86, -1.82) * mm});
            skLineSegment(sketch, "E483", {"start": v(-17.86, -1.82) * mm, "end": v(-17.8, -1.84) * mm});
            skLineSegment(sketch, "E484", {"start": v(-17.8, -1.84) * mm, "end": v(-17.76, -1.87) * mm});
            skLineSegment(sketch, "E485", {"start": v(-17.76, -1.87) * mm, "end": v(-17.72, -2.5) * mm});
            skLineSegment(sketch, "E486", {"start": v(-17.72, -2.5) * mm, "end": v(-17.75, -2.54) * mm});
            skLineSegment(sketch, "E487", {"start": v(-17.75, -2.54) * mm, "end": v(-17.8, -2.57) * mm});
            skLineSegment(sketch, "E488", {"start": v(-17.8, -2.57) * mm, "end": v(-17.99, -2.62) * mm});
            skLineSegment(sketch, "E489", {"start": v(-17.99, -2.62) * mm, "end": v(-18.16, -2.69) * mm});
            skLineSegment(sketch, "E490", {"start": v(-18.16, -2.69) * mm, "end": v(-18.36, -2.77) * mm});
            skLineSegment(sketch, "E491", {"start": v(-18.36, -2.77) * mm, "end": v(-18.59, -2.88) * mm});
            skLineSegment(sketch, "E492", {"start": v(-18.59, -2.88) * mm, "end": v(-18.83, -3) * mm});
            skLineSegment(sketch, "E493", {"start": v(-18.83, -3) * mm, "end": v(-19.08, -3.15) * mm});
            skLineSegment(sketch, "E494", {"start": v(-19.08, -3.15) * mm, "end": v(-19.06, -3.44) * mm});
            skLineSegment(sketch, "E495", {"start": v(-19.06, -3.44) * mm, "end": v(-19, -3.72) * mm});
            skLineSegment(sketch, "E496", {"start": v(-19, -3.72) * mm, "end": v(-18.73, -3.8) * mm});
            skLineSegment(sketch, "E497", {"start": v(-18.73, -3.8) * mm, "end": v(-18.46, -3.86) * mm});
            skLineSegment(sketch, "E498", {"start": v(-18.46, -3.86) * mm, "end": v(-18.21, -3.9) * mm});
            skLineSegment(sketch, "E499", {"start": v(-18.21, -3.9) * mm, "end": v(-18, -3.93) * mm});
            skLineSegment(sketch, "E500", {"start": v(-18, -3.93) * mm, "end": v(-17.81, -3.95) * mm});
            skLineSegment(sketch, "E501", {"start": v(-17.81, -3.95) * mm, "end": v(-17.63, -3.96) * mm});
            skLineSegment(sketch, "E502", {"start": v(-17.63, -3.96) * mm, "end": v(-17.56, -3.97) * mm});
            skLineSegment(sketch, "E503", {"start": v(-17.56, -3.97) * mm, "end": v(-17.52, -4) * mm});
            skLineSegment(sketch, "E504", {"start": v(-17.52, -4) * mm, "end": v(-17.4, -4.62) * mm});
            skLineSegment(sketch, "E505", {"start": v(-17.4, -4.62) * mm, "end": v(-17.42, -4.65) * mm});
            skLineSegment(sketch, "E506", {"start": v(-17.42, -4.65) * mm, "end": v(-17.48, -4.7) * mm});
            skLineSegment(sketch, "E507", {"start": v(-17.48, -4.7) * mm, "end": v(-17.65, -4.77) * mm});
            skLineSegment(sketch, "E508", {"start": v(-17.65, -4.77) * mm, "end": v(-17.81, -4.86) * mm});
            skLineSegment(sketch, "E509", {"start": v(-17.81, -4.86) * mm, "end": v(-18, -4.97) * mm});
            skLineSegment(sketch, "E510", {"start": v(-18, -4.97) * mm, "end": v(-18.21, -5.1) * mm});
            skLineSegment(sketch, "E511", {"start": v(-18.21, -5.1) * mm, "end": v(-18.44, -5.26) * mm});
            skLineSegment(sketch, "E512", {"start": v(-18.44, -5.26) * mm, "end": v(-18.66, -5.43) * mm});
            skLineSegment(sketch, "E513", {"start": v(-18.66, -5.43) * mm, "end": v(-18.6, -5.72) * mm});
            skLineSegment(sketch, "E514", {"start": v(-18.6, -5.72) * mm, "end": v(-18.51, -6) * mm});
            skLineSegment(sketch, "E515", {"start": v(-18.51, -6) * mm, "end": v(-18.23, -6.03) * mm});
            skLineSegment(sketch, "E516", {"start": v(-18.23, -6.03) * mm, "end": v(-17.95, -6.06) * mm});
            skLineSegment(sketch, "E517", {"start": v(-17.95, -6.06) * mm, "end": v(-17.7, -6.07) * mm});
            skLineSegment(sketch, "E518", {"start": v(-17.7, -6.07) * mm, "end": v(-17.49, -6.07) * mm});
            skLineSegment(sketch, "E519", {"start": v(-17.49, -6.07) * mm, "end": v(-17.3, -6.06) * mm});
            skLineSegment(sketch, "E520", {"start": v(-17.3, -6.06) * mm, "end": v(-17.12, -6.05) * mm});
            skLineSegment(sketch, "E521", {"start": v(-17.12, -6.05) * mm, "end": v(-17.05, -6.05) * mm});
            skLineSegment(sketch, "E522", {"start": v(-17.05, -6.05) * mm, "end": v(-17, -6.07) * mm});
            skLineSegment(sketch, "E523", {"start": v(-17, -6.07) * mm, "end": v(-16.8, -6.67) * mm});
            skLineSegment(sketch, "E524", {"start": v(-16.8, -6.67) * mm, "end": v(-16.82, -6.71) * mm});
            skLineSegment(sketch, "E525", {"start": v(-16.82, -6.71) * mm, "end": v(-16.88, -6.76) * mm});
            skLineSegment(sketch, "E526", {"start": v(-16.88, -6.76) * mm, "end": v(-17.03, -6.86) * mm});
            skLineSegment(sketch, "E527", {"start": v(-17.03, -6.86) * mm, "end": v(-17.18, -6.97) * mm});
            skLineSegment(sketch, "E528", {"start": v(-17.18, -6.97) * mm, "end": v(-17.36, -7.1) * mm});
            skLineSegment(sketch, "E529", {"start": v(-17.36, -7.1) * mm, "end": v(-17.55, -7.26) * mm});
            skLineSegment(sketch, "E530", {"start": v(-17.55, -7.26) * mm, "end": v(-17.75, -7.45) * mm});
            skLineSegment(sketch, "E531", {"start": v(-17.75, -7.45) * mm, "end": v(-17.95, -7.65) * mm});
            skLineSegment(sketch, "E532", {"start": v(-17.95, -7.65) * mm, "end": v(-17.86, -7.92) * mm});
            skLineSegment(sketch, "E533", {"start": v(-17.86, -7.92) * mm, "end": v(-17.73, -8.18) * mm});
            skLineSegment(sketch, "E534", {"start": v(-17.73, -8.18) * mm, "end": v(-17.45, -8.18) * mm});
            skLineSegment(sketch, "E535", {"start": v(-17.45, -8.18) * mm, "end": v(-17.17, -8.17) * mm});
            skLineSegment(sketch, "E536", {"start": v(-17.17, -8.17) * mm, "end": v(-16.92, -8.15) * mm});
            skLineSegment(sketch, "E537", {"start": v(-16.92, -8.15) * mm, "end": v(-16.7, -8.12) * mm});
            skLineSegment(sketch, "E538", {"start": v(-16.7, -8.12) * mm, "end": v(-16.52, -8.1) * mm});
            skLineSegment(sketch, "E539", {"start": v(-16.52, -8.1) * mm, "end": v(-16.34, -8.05) * mm});
            skLineSegment(sketch, "E540", {"start": v(-16.34, -8.05) * mm, "end": v(-16.27, -8.05) * mm});
            skLineSegment(sketch, "E541", {"start": v(-16.27, -8.05) * mm, "end": v(-16.23, -8.06) * mm});
            skLineSegment(sketch, "E542", {"start": v(-16.23, -8.06) * mm, "end": v(-15.95, -8.63) * mm});
            skLineSegment(sketch, "E543", {"start": v(-15.95, -8.63) * mm, "end": v(-15.96, -8.67) * mm});
            skLineSegment(sketch, "E544", {"start": v(-15.96, -8.67) * mm, "end": v(-16, -8.73) * mm});
            skLineSegment(sketch, "E545", {"start": v(-16, -8.73) * mm, "end": v(-16.15, -8.84) * mm});
            skLineSegment(sketch, "E546", {"start": v(-16.15, -8.84) * mm, "end": v(-16.29, -8.97) * mm});
            skLineSegment(sketch, "E547", {"start": v(-16.29, -8.97) * mm, "end": v(-16.44, -9.13) * mm});
            skLineSegment(sketch, "E548", {"start": v(-16.44, -9.13) * mm, "end": v(-16.6, -9.3) * mm});
            skLineSegment(sketch, "E549", {"start": v(-16.6, -9.3) * mm, "end": v(-16.79, -9.52) * mm});
            skLineSegment(sketch, "E550", {"start": v(-16.79, -9.52) * mm, "end": v(-16.96, -9.75) * mm});
            skLineSegment(sketch, "E551", {"start": v(-16.96, -9.75) * mm, "end": v(-16.83, -10) * mm});
            skLineSegment(sketch, "E552", {"start": v(-16.83, -10) * mm, "end": v(-16.67, -10.25) * mm});
            skLineSegment(sketch, "E553", {"start": v(-16.67, -10.25) * mm, "end": v(-16.39, -10.21) * mm});
            skLineSegment(sketch, "E554", {"start": v(-16.39, -10.21) * mm, "end": v(-16.11, -10.17) * mm});
            skLineSegment(sketch, "E555", {"start": v(-16.11, -10.17) * mm, "end": v(-15.87, -10.11) * mm});
            skLineSegment(sketch, "E556", {"start": v(-15.87, -10.11) * mm, "end": v(-15.66, -10.06) * mm});
            skLineSegment(sketch, "E557", {"start": v(-15.66, -10.06) * mm, "end": v(-15.48, -10) * mm});
            skLineSegment(sketch, "E558", {"start": v(-15.48, -10) * mm, "end": v(-15.3, -9.94) * mm});
            skLineSegment(sketch, "E559", {"start": v(-15.3, -9.94) * mm, "end": v(-15.24, -9.92) * mm});
            skLineSegment(sketch, "E560", {"start": v(-15.24, -9.92) * mm, "end": v(-15.2, -9.93) * mm});
            skLineSegment(sketch, "E561", {"start": v(-15.2, -9.93) * mm, "end": v(-14.84, -10.46) * mm});
            skLineSegment(sketch, "E562", {"start": v(-14.84, -10.46) * mm, "end": v(-14.85, -10.5) * mm});
            skLineSegment(sketch, "E563", {"start": v(-14.85, -10.5) * mm, "end": v(-14.89, -10.56) * mm});
            skLineSegment(sketch, "E564", {"start": v(-14.89, -10.56) * mm, "end": v(-15.01, -10.7) * mm});
            skLineSegment(sketch, "E565", {"start": v(-15.01, -10.7) * mm, "end": v(-15.13, -10.84) * mm});
            skLineSegment(sketch, "E566", {"start": v(-15.13, -10.84) * mm, "end": v(-15.27, -11.02) * mm});
            skLineSegment(sketch, "E567", {"start": v(-15.27, -11.02) * mm, "end": v(-15.4, -11.22) * mm});
            skLineSegment(sketch, "E568", {"start": v(-15.4, -11.22) * mm, "end": v(-15.56, -11.46) * mm});
            skLineSegment(sketch, "E569", {"start": v(-15.56, -11.46) * mm, "end": v(-15.7, -11.7) * mm});
            skLineSegment(sketch, "E570", {"start": v(-15.7, -11.7) * mm, "end": v(-15.54, -11.94) * mm});
            skLineSegment(sketch, "E571", {"start": v(-15.54, -11.94) * mm, "end": v(-15.34, -12.16) * mm});
            skLineSegment(sketch, "E572", {"start": v(-15.34, -12.16) * mm, "end": v(-15.07, -12.09) * mm});
            skLineSegment(sketch, "E573", {"start": v(-15.07, -12.09) * mm, "end": v(-14.8, -12) * mm});
            skLineSegment(sketch, "E574", {"start": v(-14.8, -12) * mm, "end": v(-14.57, -11.92) * mm});
            skLineSegment(sketch, "E575", {"start": v(-14.57, -11.92) * mm, "end": v(-14.37, -11.84) * mm});
            skLineSegment(sketch, "E576", {"start": v(-14.37, -11.84) * mm, "end": v(-14.2, -11.76) * mm});
            skLineSegment(sketch, "E577", {"start": v(-14.2, -11.76) * mm, "end": v(-14.04, -11.67) * mm});
            skLineSegment(sketch, "E578", {"start": v(-14.04, -11.67) * mm, "end": v(-13.97, -11.65) * mm});
            skLineSegment(sketch, "E579", {"start": v(-13.97, -11.65) * mm, "end": v(-13.93, -11.66) * mm});
            skLineSegment(sketch, "E580", {"start": v(-13.93, -11.66) * mm, "end": v(-13.5, -12.13) * mm});
            skLineSegment(sketch, "E581", {"start": v(-13.5, -12.13) * mm, "end": v(-13.51, -12.18) * mm});
            skLineSegment(sketch, "E582", {"start": v(-13.51, -12.18) * mm, "end": v(-13.54, -12.24) * mm});
            skLineSegment(sketch, "E583", {"start": v(-13.54, -12.24) * mm, "end": v(-13.65, -12.4) * mm});
            skLineSegment(sketch, "E584", {"start": v(-13.65, -12.4) * mm, "end": v(-13.75, -12.55) * mm});
            skLineSegment(sketch, "E585", {"start": v(-13.75, -12.55) * mm, "end": v(-13.86, -12.74) * mm});
            skLineSegment(sketch, "E586", {"start": v(-13.86, -12.74) * mm, "end": v(-13.97, -12.96) * mm});
            skLineSegment(sketch, "E587", {"start": v(-13.97, -12.96) * mm, "end": v(-14.09, -13.21) * mm});
            skLineSegment(sketch, "E588", {"start": v(-14.09, -13.21) * mm, "end": v(-14.2, -13.47) * mm});
            skLineSegment(sketch, "E589", {"start": v(-14.2, -13.47) * mm, "end": v(-14, -13.7) * mm});
            skLineSegment(sketch, "E590", {"start": v(-14, -13.7) * mm, "end": v(-13.78, -13.88) * mm});
            skLineSegment(sketch, "E591", {"start": v(-13.78, -13.88) * mm, "end": v(-13.52, -13.78) * mm});
            skLineSegment(sketch, "E592", {"start": v(-13.52, -13.78) * mm, "end": v(-13.27, -13.66) * mm});
            skLineSegment(sketch, "E593", {"start": v(-13.27, -13.66) * mm, "end": v(-13.05, -13.54) * mm});
            skLineSegment(sketch, "E594", {"start": v(-13.05, -13.54) * mm, "end": v(-12.86, -13.44) * mm});
            skLineSegment(sketch, "E595", {"start": v(-12.86, -13.44) * mm, "end": v(-12.7, -13.33) * mm});
            skLineSegment(sketch, "E596", {"start": v(-12.7, -13.33) * mm, "end": v(-12.55, -13.23) * mm});
            skLineSegment(sketch, "E597", {"start": v(-12.55, -13.23) * mm, "end": v(-12.49, -13.2) * mm});
            skLineSegment(sketch, "E598", {"start": v(-12.49, -13.2) * mm, "end": v(-12.45, -13.2) * mm});
            skLineSegment(sketch, "E599", {"start": v(-12.45, -13.2) * mm, "end": v(-11.97, -13.62) * mm});
            skLineSegment(sketch, "E600", {"start": v(-11.97, -13.62) * mm, "end": v(-11.96, -13.66) * mm});
            skLineSegment(sketch, "E601", {"start": v(-11.96, -13.66) * mm, "end": v(-11.99, -13.73) * mm});
            skLineSegment(sketch, "E602", {"start": v(-11.99, -13.73) * mm, "end": v(-12.07, -13.89) * mm});
            skLineSegment(sketch, "E603", {"start": v(-12.07, -13.89) * mm, "end": v(-12.15, -14.06) * mm});
            skLineSegment(sketch, "E604", {"start": v(-12.15, -14.06) * mm, "end": v(-12.23, -14.26) * mm});
            skLineSegment(sketch, "E605", {"start": v(-12.23, -14.26) * mm, "end": v(-12.32, -14.5) * mm});
            skLineSegment(sketch, "E606", {"start": v(-12.32, -14.5) * mm, "end": v(-12.4, -14.76) * mm});
            skLineSegment(sketch, "E607", {"start": v(-12.4, -14.76) * mm, "end": v(-12.47, -15.03) * mm});
            skLineSegment(sketch, "E608", {"start": v(-12.47, -15.03) * mm, "end": v(-12.25, -15.22) * mm});
            skLineSegment(sketch, "E609", {"start": v(-12.25, -15.22) * mm, "end": v(-12.01, -15.39) * mm});
            skLineSegment(sketch, "E610", {"start": v(-12.01, -15.39) * mm, "end": v(-11.77, -15.25) * mm});
            skLineSegment(sketch, "E611", {"start": v(-11.77, -15.25) * mm, "end": v(-11.53, -15.1) * mm});
            skLineSegment(sketch, "E612", {"start": v(-11.53, -15.1) * mm, "end": v(-11.33, -14.95) * mm});
            skLineSegment(sketch, "E613", {"start": v(-11.33, -14.95) * mm, "end": v(-11.16, -14.82) * mm});
            skLineSegment(sketch, "E614", {"start": v(-11.16, -14.82) * mm, "end": v(-11.01, -14.7) * mm});
            skLineSegment(sketch, "E615", {"start": v(-11.01, -14.7) * mm, "end": v(-10.88, -14.58) * mm});
            skLineSegment(sketch, "E616", {"start": v(-10.88, -14.58) * mm, "end": v(-10.82, -14.54) * mm});
            skLineSegment(sketch, "E617", {"start": v(-10.82, -14.54) * mm, "end": v(-10.77, -14.53) * mm});
            skLineSegment(sketch, "E618", {"start": v(-10.77, -14.53) * mm, "end": v(-10.25, -14.88) * mm});
            skLineSegment(sketch, "E619", {"start": v(-10.25, -14.88) * mm, "end": v(-10.24, -14.93) * mm});
            skLineSegment(sketch, "E620", {"start": v(-10.24, -14.93) * mm, "end": v(-10.25, -15) * mm});
            skLineSegment(sketch, "E621", {"start": v(-10.25, -15) * mm, "end": v(-10.31, -15.17) * mm});
            skLineSegment(sketch, "E622", {"start": v(-10.31, -15.17) * mm, "end": v(-10.37, -15.35) * mm});
            skLineSegment(sketch, "E623", {"start": v(-10.37, -15.35) * mm, "end": v(-10.42, -15.56) * mm});
            skLineSegment(sketch, "E624", {"start": v(-10.42, -15.56) * mm, "end": v(-10.48, -15.8) * mm});
            skLineSegment(sketch, "E625", {"start": v(-10.48, -15.8) * mm, "end": v(-10.53, -16.08) * mm});
            skLineSegment(sketch, "E626", {"start": v(-10.53, -16.08) * mm, "end": v(-10.56, -16.35) * mm});
            skLineSegment(sketch, "E627", {"start": v(-10.56, -16.35) * mm, "end": v(-10.32, -16.52) * mm});
            skLineSegment(sketch, "E628", {"start": v(-10.32, -16.52) * mm, "end": v(-10.06, -16.64) * mm});
            skLineSegment(sketch, "E629", {"start": v(-10.06, -16.64) * mm, "end": v(-9.84, -16.47) * mm});
            skLineSegment(sketch, "E630", {"start": v(-9.84, -16.47) * mm, "end": v(-9.62, -16.3) * mm});
            skLineSegment(sketch, "E631", {"start": v(-9.62, -16.3) * mm, "end": v(-9.44, -16.13) * mm});
            skLineSegment(sketch, "E632", {"start": v(-9.44, -16.13) * mm, "end": v(-9.28, -15.97) * mm});
            skLineSegment(sketch, "E633", {"start": v(-9.28, -15.97) * mm, "end": v(-9.16, -15.84) * mm});
            skLineSegment(sketch, "E634", {"start": v(-9.16, -15.84) * mm, "end": v(-9.04, -15.7) * mm});
            skLineSegment(sketch, "E635", {"start": v(-9.04, -15.7) * mm, "end": v(-8.99, -15.65) * mm});
            skLineSegment(sketch, "E636", {"start": v(-8.99, -15.65) * mm, "end": v(-8.94, -15.64) * mm});
            skLineSegment(sketch, "E637", {"start": v(-8.94, -15.64) * mm, "end": v(-8.37, -15.92) * mm});
            skLineSegment(sketch, "E638", {"start": v(-8.37, -15.92) * mm, "end": v(-8.36, -15.96) * mm});
            skLineSegment(sketch, "E639", {"start": v(-8.36, -15.96) * mm, "end": v(-8.36, -16.03) * mm});
            skLineSegment(sketch, "E640", {"start": v(-8.36, -16.03) * mm, "end": v(-8.4, -16.2) * mm});
            skLineSegment(sketch, "E641", {"start": v(-8.4, -16.2) * mm, "end": v(-8.43, -16.4) * mm});
            skLineSegment(sketch, "E642", {"start": v(-8.43, -16.4) * mm, "end": v(-8.46, -16.6) * mm});
            skLineSegment(sketch, "E643", {"start": v(-8.46, -16.6) * mm, "end": v(-8.48, -16.86) * mm});
            skLineSegment(sketch, "E644", {"start": v(-8.48, -16.86) * mm, "end": v(-8.5, -17.14) * mm});
            skLineSegment(sketch, "E645", {"start": v(-8.5, -17.14) * mm, "end": v(-8.5, -17.42) * mm});
            skLineSegment(sketch, "E646", {"start": v(-8.5, -17.42) * mm, "end": v(-8.23, -17.55) * mm});
            skLineSegment(sketch, "E647", {"start": v(-8.23, -17.55) * mm, "end": v(-7.96, -17.64) * mm});
            skLineSegment(sketch, "E648", {"start": v(-7.96, -17.64) * mm, "end": v(-7.76, -17.44) * mm});
            skLineSegment(sketch, "E649", {"start": v(-7.76, -17.44) * mm, "end": v(-7.57, -17.23) * mm});
            skLineSegment(sketch, "E650", {"start": v(-7.57, -17.23) * mm, "end": v(-7.41, -17.04) * mm});
            skLineSegment(sketch, "E651", {"start": v(-7.41, -17.04) * mm, "end": v(-7.28, -16.87) * mm});
            skLineSegment(sketch, "E652", {"start": v(-7.28, -16.87) * mm, "end": v(-7.17, -16.72) * mm});
            skLineSegment(sketch, "E653", {"start": v(-7.17, -16.72) * mm, "end": v(-7.07, -16.56) * mm});
            skLineSegment(sketch, "E654", {"start": v(-7.07, -16.56) * mm, "end": v(-7.02, -16.51) * mm});
            skLineSegment(sketch, "E655", {"start": v(-7.02, -16.51) * mm, "end": v(-6.98, -16.5) * mm});
            skLineSegment(sketch, "E656", {"start": v(-6.98, -16.5) * mm, "end": v(-6.38, -16.7) * mm});
            skLineSegment(sketch, "E657", {"start": v(-6.38, -16.7) * mm, "end": v(-6.36, -16.74) * mm});
            skLineSegment(sketch, "E658", {"start": v(-6.36, -16.74) * mm, "end": v(-6.36, -16.8) * mm});
            skLineSegment(sketch, "E659", {"start": v(-6.36, -16.8) * mm, "end": v(-6.37, -16.99) * mm});
            skLineSegment(sketch, "E660", {"start": v(-6.37, -16.99) * mm, "end": v(-6.38, -17.18) * mm});
            skLineSegment(sketch, "E661", {"start": v(-6.38, -17.18) * mm, "end": v(-6.38, -17.4) * mm});
            skLineSegment(sketch, "E662", {"start": v(-6.38, -17.4) * mm, "end": v(-6.37, -17.64) * mm});
            skLineSegment(sketch, "E663", {"start": v(-6.37, -17.64) * mm, "end": v(-6.34, -17.92) * mm});
            skLineSegment(sketch, "E664", {"start": v(-6.34, -17.92) * mm, "end": v(-6.3, -18.2) * mm});
            skLineSegment(sketch, "E665", {"start": v(-6.3, -18.2) * mm, "end": v(-6.03, -18.3) * mm});
            skLineSegment(sketch, "E666", {"start": v(-6.03, -18.3) * mm, "end": v(-5.75, -18.35) * mm});
            skLineSegment(sketch, "E667", {"start": v(-5.75, -18.35) * mm, "end": v(-5.57, -18.13) * mm});
            skLineSegment(sketch, "E668", {"start": v(-5.57, -18.13) * mm, "end": v(-5.41, -17.9) * mm});
            skLineSegment(sketch, "E669", {"start": v(-5.41, -17.9) * mm, "end": v(-5.28, -17.69) * mm});
            skLineSegment(sketch, "E670", {"start": v(-5.28, -17.69) * mm, "end": v(-5.17, -17.5) * mm});
            skLineSegment(sketch, "E671", {"start": v(-5.17, -17.5) * mm, "end": v(-5.08, -17.34) * mm});
            skLineSegment(sketch, "E672", {"start": v(-5.08, -17.34) * mm, "end": v(-5, -17.17) * mm});
            skLineSegment(sketch, "E673", {"start": v(-5, -17.17) * mm, "end": v(-4.97, -17.11) * mm});
            skLineSegment(sketch, "E674", {"start": v(-4.97, -17.11) * mm, "end": v(-4.93, -17.09) * mm});
            skLineSegment(sketch, "E675", {"start": v(-4.93, -17.09) * mm, "end": v(-4.3, -17.21) * mm});
            skLineSegment(sketch, "E676", {"start": v(-4.3, -17.21) * mm, "end": v(-4.28, -17.25) * mm});
            skLineSegment(sketch, "E677", {"start": v(-4.28, -17.25) * mm, "end": v(-4.27, -17.31) * mm});
            skLineSegment(sketch, "E678", {"start": v(-4.27, -17.31) * mm, "end": v(-4.26, -17.5) * mm});
            skLineSegment(sketch, "E679", {"start": v(-4.26, -17.5) * mm, "end": v(-4.24, -17.69) * mm});
            skLineSegment(sketch, "E680", {"start": v(-4.24, -17.69) * mm, "end": v(-4.21, -17.9) * mm});
            skLineSegment(sketch, "E681", {"start": v(-4.21, -17.9) * mm, "end": v(-4.17, -18.15) * mm});
            skLineSegment(sketch, "E682", {"start": v(-4.17, -18.15) * mm, "end": v(-4.1, -18.42) * mm});
            skLineSegment(sketch, "E683", {"start": v(-4.1, -18.42) * mm, "end": v(-4.04, -18.69) * mm});
            skLineSegment(sketch, "E684", {"start": v(-4.04, -18.69) * mm, "end": v(-3.75, -18.75) * mm});
            skLineSegment(sketch, "E685", {"start": v(-3.75, -18.75) * mm, "end": v(-3.46, -18.77) * mm});
            skLineSegment(sketch, "E686", {"start": v(-3.46, -18.77) * mm, "end": v(-3.32, -18.52) * mm});
            skLineSegment(sketch, "E687", {"start": v(-3.32, -18.52) * mm, "end": v(-3.19, -18.27) * mm});
            skLineSegment(sketch, "E688", {"start": v(-3.19, -18.27) * mm, "end": v(-3.08, -18.05) * mm});
            skLineSegment(sketch, "E689", {"start": v(-3.08, -18.05) * mm, "end": v(-3, -17.85) * mm});
            skLineSegment(sketch, "E690", {"start": v(-3, -17.85) * mm, "end": v(-2.94, -17.67) * mm});
            skLineSegment(sketch, "E691", {"start": v(-2.94, -17.67) * mm, "end": v(-2.88, -17.5) * mm});
            skLineSegment(sketch, "E692", {"start": v(-2.88, -17.5) * mm, "end": v(-2.85, -17.43) * mm});
            skLineSegment(sketch, "E693", {"start": v(-2.85, -17.43) * mm, "end": v(-2.82, -17.4) * mm});
            skLineSegment(sketch, "E694", {"start": v(-2.82, -17.4) * mm, "end": v(-2.18, -17.45) * mm});
            skLineSegment(sketch, "E695", {"start": v(-2.18, -17.45) * mm, "end": v(-2.15, -17.48) * mm});
            skLineSegment(sketch, "E696", {"start": v(-2.15, -17.48) * mm, "end": v(-2.13, -17.55) * mm});
            skLineSegment(sketch, "E697", {"start": v(-2.13, -17.55) * mm, "end": v(-2.1, -17.73) * mm});
            skLineSegment(sketch, "E698", {"start": v(-2.1, -17.73) * mm, "end": v(-2.06, -17.91) * mm});
            skLineSegment(sketch, "E699", {"start": v(-2.06, -17.91) * mm, "end": v(-2, -18.12) * mm});
            skLineSegment(sketch, "E700", {"start": v(-2, -18.12) * mm, "end": v(-1.92, -18.36) * mm});
            skLineSegment(sketch, "E701", {"start": v(-1.92, -18.36) * mm, "end": v(-1.83, -18.62) * mm});
            skLineSegment(sketch, "E702", {"start": v(-1.83, -18.62) * mm, "end": v(-1.72, -18.88) * mm});
            skLineSegment(sketch, "E703", {"start": v(-1.72, -18.88) * mm, "end": v(-1.43, -18.9) * mm});
            skLineSegment(sketch, "E704", {"start": v(-1.43, -18.9) * mm, "end": v(-1.14, -18.88) * mm});
            skLineSegment(sketch, "E705", {"start": v(-1.14, -18.88) * mm, "end": v(-1.03, -18.62) * mm});
            skLineSegment(sketch, "E706", {"start": v(-1.03, -18.62) * mm, "end": v(-0.94, -18.36) * mm});
            skLineSegment(sketch, "E707", {"start": v(-0.94, -18.36) * mm, "end": v(-0.86, -18.12) * mm});
            skLineSegment(sketch, "E708", {"start": v(-0.86, -18.12) * mm, "end": v(-0.8, -17.91) * mm});
            skLineSegment(sketch, "E709", {"start": v(-0.8, -17.91) * mm, "end": v(-0.76, -17.73) * mm});
            skLineSegment(sketch, "E710", {"start": v(-0.76, -17.73) * mm, "end": v(-0.73, -17.55) * mm});
            skLineSegment(sketch, "E711", {"start": v(-0.73, -17.55) * mm, "end": v(-0.7, -17.48) * mm});
            skLineSegment(sketch, "E712", {"start": v(-0.7, -17.48) * mm, "end": v(-0.68, -17.45) * mm});
            skLineSegment(sketch, "E713", {"start": v(-0.68, -17.45) * mm, "end": v(-0.04, -17.4) * mm});
            skLineSegment(sketch, "E714", {"start": v(-0.04, -17.4) * mm, "end": v(-0.01, -17.43) * mm});
            skLineSegment(sketch, "E715", {"start": v(-0.01, -17.43) * mm, "end": v(0.02, -17.5) * mm});
            skLineSegment(sketch, "E716", {"start": v(0.02, -17.5) * mm, "end": v(0.08, -17.67) * mm});
            skLineSegment(sketch, "E717", {"start": v(0.08, -17.67) * mm, "end": v(0.14, -17.85) * mm});
            skLineSegment(sketch, "E718", {"start": v(0.14, -17.85) * mm, "end": v(0.23, -18.05) * mm});
            skLineSegment(sketch, "E719", {"start": v(0.23, -18.05) * mm, "end": v(0.33, -18.27) * mm});
            skLineSegment(sketch, "E720", {"start": v(0.33, -18.27) * mm, "end": v(0.46, -18.52) * mm});
            skLineSegment(sketch, "E721", {"start": v(0.46, -18.52) * mm, "end": v(0.6, -18.77) * mm});
            skLineSegment(sketch, "E722", {"start": v(0.6, -18.77) * mm, "end": v(0.9, -18.75) * mm});
            skLineSegment(sketch, "E723", {"start": v(0.9, -18.75) * mm, "end": v(1.18, -18.69) * mm});
            skLineSegment(sketch, "E724", {"start": v(1.18, -18.69) * mm, "end": v(1.25, -18.42) * mm});
            skLineSegment(sketch, "E725", {"start": v(1.25, -18.42) * mm, "end": v(1.31, -18.15) * mm});
            skLineSegment(sketch, "E726", {"start": v(1.31, -18.15) * mm, "end": v(1.35, -17.9) * mm});
            skLineSegment(sketch, "E727", {"start": v(1.35, -17.9) * mm, "end": v(1.38, -17.69) * mm});
            skLineSegment(sketch, "E728", {"start": v(1.38, -17.69) * mm, "end": v(1.4, -17.5) * mm});
            skLineSegment(sketch, "E729", {"start": v(1.4, -17.5) * mm, "end": v(1.4, -17.31) * mm});
            skLineSegment(sketch, "E730", {"start": v(1.4, -17.31) * mm, "end": v(1.42, -17.25) * mm});
            skLineSegment(sketch, "E731", {"start": v(1.42, -17.25) * mm, "end": v(1.45, -17.21) * mm});
            skLineSegment(sketch, "E732", {"start": v(1.45, -17.21) * mm, "end": v(2.07, -17.09) * mm});
            skLineSegment(sketch, "E733", {"start": v(2.07, -17.09) * mm, "end": v(2.1, -17.11) * mm});
            skLineSegment(sketch, "E734", {"start": v(2.1, -17.11) * mm, "end": v(2.15, -17.17) * mm});
            skLineSegment(sketch, "E735", {"start": v(2.15, -17.17) * mm, "end": v(2.23, -17.34) * mm});
            skLineSegment(sketch, "E736", {"start": v(2.23, -17.34) * mm, "end": v(2.31, -17.5) * mm});
            skLineSegment(sketch, "E737", {"start": v(2.31, -17.5) * mm, "end": v(2.42, -17.69) * mm});
            skLineSegment(sketch, "E738", {"start": v(2.42, -17.69) * mm, "end": v(2.56, -17.9) * mm});
            skLineSegment(sketch, "E739", {"start": v(2.56, -17.9) * mm, "end": v(2.72, -18.13) * mm});
            skLineSegment(sketch, "E740", {"start": v(2.72, -18.13) * mm, "end": v(2.89, -18.35) * mm});
            skLineSegment(sketch, "E741", {"start": v(2.89, -18.35) * mm, "end": v(3.17, -18.3) * mm});
            skLineSegment(sketch, "E742", {"start": v(3.17, -18.3) * mm, "end": v(3.45, -18.2) * mm});
            skLineSegment(sketch, "E743", {"start": v(3.45, -18.2) * mm, "end": v(3.49, -17.92) * mm});
            skLineSegment(sketch, "E744", {"start": v(3.49, -17.92) * mm, "end": v(3.51, -17.64) * mm});
            skLineSegment(sketch, "E745", {"start": v(3.51, -17.64) * mm, "end": v(3.52, -17.4) * mm});
            skLineSegment(sketch, "E746", {"start": v(3.52, -17.4) * mm, "end": v(3.52, -17.18) * mm});
            skLineSegment(sketch, "E747", {"start": v(3.52, -17.18) * mm, "end": v(3.51, -16.99) * mm});
            skLineSegment(sketch, "E748", {"start": v(3.51, -16.99) * mm, "end": v(3.5, -16.8) * mm});
            skLineSegment(sketch, "E749", {"start": v(3.5, -16.8) * mm, "end": v(3.5, -16.74) * mm});
            skLineSegment(sketch, "E750", {"start": v(3.5, -16.74) * mm, "end": v(3.52, -16.7) * mm});
            skLineSegment(sketch, "E751", {"start": v(3.52, -16.7) * mm, "end": v(4.13, -16.5) * mm});
            skLineSegment(sketch, "E752", {"start": v(4.13, -16.5) * mm, "end": v(4.16, -16.51) * mm});
            skLineSegment(sketch, "E753", {"start": v(4.16, -16.51) * mm, "end": v(4.21, -16.56) * mm});
            skLineSegment(sketch, "E754", {"start": v(4.21, -16.56) * mm, "end": v(4.31, -16.72) * mm});
            skLineSegment(sketch, "E755", {"start": v(4.31, -16.72) * mm, "end": v(4.42, -16.87) * mm});
            skLineSegment(sketch, "E756", {"start": v(4.42, -16.87) * mm, "end": v(4.55, -17.04) * mm});
            skLineSegment(sketch, "E757", {"start": v(4.55, -17.04) * mm, "end": v(4.71, -17.23) * mm});
            skLineSegment(sketch, "E758", {"start": v(4.71, -17.23) * mm, "end": v(4.9, -17.44) * mm});
            skLineSegment(sketch, "E759", {"start": v(4.9, -17.44) * mm, "end": v(5.1, -17.64) * mm});
            skLineSegment(sketch, "E760", {"start": v(5.1, -17.64) * mm, "end": v(5.38, -17.55) * mm});
            skLineSegment(sketch, "E761", {"start": v(5.38, -17.55) * mm, "end": v(5.64, -17.42) * mm});
            skLineSegment(sketch, "E762", {"start": v(5.64, -17.42) * mm, "end": v(5.64, -17.14) * mm});
            skLineSegment(sketch, "E763", {"start": v(5.64, -17.14) * mm, "end": v(5.62, -16.86) * mm});
            skLineSegment(sketch, "E764", {"start": v(5.62, -16.86) * mm, "end": v(5.6, -16.6) * mm});
            skLineSegment(sketch, "E765", {"start": v(5.6, -16.6) * mm, "end": v(5.58, -16.4) * mm});
            skLineSegment(sketch, "E766", {"start": v(5.58, -16.4) * mm, "end": v(5.54, -16.2) * mm});
            skLineSegment(sketch, "E767", {"start": v(5.54, -16.2) * mm, "end": v(5.5, -16.03) * mm});
            skLineSegment(sketch, "E768", {"start": v(5.5, -16.03) * mm, "end": v(5.5, -15.96) * mm});
            skLineSegment(sketch, "E769", {"start": v(5.5, -15.96) * mm, "end": v(5.51, -15.92) * mm});
            skLineSegment(sketch, "E770", {"start": v(5.51, -15.92) * mm, "end": v(6.08, -15.64) * mm});
            skLineSegment(sketch, "E771", {"start": v(6.08, -15.64) * mm, "end": v(6.13, -15.65) * mm});
            skLineSegment(sketch, "E772", {"start": v(6.13, -15.65) * mm, "end": v(6.18, -15.7) * mm});
            skLineSegment(sketch, "E773", {"start": v(6.18, -15.7) * mm, "end": v(6.3, -15.84) * mm});
            skLineSegment(sketch, "E774", {"start": v(6.3, -15.84) * mm, "end": v(6.42, -15.97) * mm});
            skLineSegment(sketch, "E775", {"start": v(6.42, -15.97) * mm, "end": v(6.58, -16.13) * mm});
            skLineSegment(sketch, "E776", {"start": v(6.58, -16.13) * mm, "end": v(6.76, -16.3) * mm});
            skLineSegment(sketch, "E777", {"start": v(6.76, -16.3) * mm, "end": v(6.98, -16.47) * mm});
            skLineSegment(sketch, "E778", {"start": v(6.98, -16.47) * mm, "end": v(7.2, -16.64) * mm});
            skLineSegment(sketch, "E779", {"start": v(7.2, -16.64) * mm, "end": v(7.46, -16.52) * mm});
            skLineSegment(sketch, "E780", {"start": v(7.46, -16.52) * mm, "end": v(7.7, -16.35) * mm});
            skLineSegment(sketch, "E781", {"start": v(7.7, -16.35) * mm, "end": v(7.67, -16.08) * mm});
            skLineSegment(sketch, "E782", {"start": v(7.67, -16.08) * mm, "end": v(7.62, -15.8) * mm});
            skLineSegment(sketch, "E783", {"start": v(7.62, -15.8) * mm, "end": v(7.57, -15.56) * mm});
            skLineSegment(sketch, "E784", {"start": v(7.57, -15.56) * mm, "end": v(7.5, -15.35) * mm});
            skLineSegment(sketch, "E785", {"start": v(7.5, -15.35) * mm, "end": v(7.45, -15.17) * mm});
            skLineSegment(sketch, "E786", {"start": v(7.45, -15.17) * mm, "end": v(7.4, -15) * mm});
            skLineSegment(sketch, "E787", {"start": v(7.4, -15) * mm, "end": v(7.38, -14.93) * mm});
            skLineSegment(sketch, "E788", {"start": v(7.38, -14.93) * mm, "end": v(7.39, -14.88) * mm});
            skLineSegment(sketch, "E789", {"start": v(7.39, -14.88) * mm, "end": v(7.92, -14.53) * mm});
            skLineSegment(sketch, "E790", {"start": v(7.92, -14.53) * mm, "end": v(7.96, -14.54) * mm});
            skLineSegment(sketch, "E791", {"start": v(7.96, -14.54) * mm, "end": v(8.02, -14.58) * mm});
            skLineSegment(sketch, "E792", {"start": v(8.02, -14.58) * mm, "end": v(8.15, -14.7) * mm});
            skLineSegment(sketch, "E793", {"start": v(8.15, -14.7) * mm, "end": v(8.3, -14.82) * mm});
            skLineSegment(sketch, "E794", {"start": v(8.3, -14.82) * mm, "end": v(8.47, -14.95) * mm});
            skLineSegment(sketch, "E795", {"start": v(8.47, -14.95) * mm, "end": v(8.67, -15.1) * mm});
            skLineSegment(sketch, "E796", {"start": v(8.67, -15.1) * mm, "end": v(8.9, -15.25) * mm});
            skLineSegment(sketch, "E797", {"start": v(8.9, -15.25) * mm, "end": v(9.15, -15.39) * mm});
            skLineSegment(sketch, "E798", {"start": v(9.15, -15.39) * mm, "end": v(9.4, -15.22) * mm});
            skLineSegment(sketch, "E799", {"start": v(9.4, -15.22) * mm, "end": v(9.61, -15.03) * mm});
            skLineSegment(sketch, "E800", {"start": v(9.61, -15.03) * mm, "end": v(9.54, -14.76) * mm});
            skLineSegment(sketch, "E801", {"start": v(9.54, -14.76) * mm, "end": v(9.46, -14.5) * mm});
            skLineSegment(sketch, "E802", {"start": v(9.46, -14.5) * mm, "end": v(9.37, -14.26) * mm});
            skLineSegment(sketch, "E803", {"start": v(9.37, -14.26) * mm, "end": v(9.3, -14.06) * mm});
            skLineSegment(sketch, "E804", {"start": v(9.3, -14.06) * mm, "end": v(9.21, -13.89) * mm});
            skLineSegment(sketch, "E805", {"start": v(9.21, -13.89) * mm, "end": v(9.13, -13.73) * mm});
            skLineSegment(sketch, "E806", {"start": v(9.13, -13.73) * mm, "end": v(9.1, -13.66) * mm});
            skLineSegment(sketch, "E807", {"start": v(9.1, -13.66) * mm, "end": v(9.1, -13.62) * mm});
            skLineSegment(sketch, "E808", {"start": v(9.1, -13.62) * mm, "end": v(9.59, -13.2) * mm});
            skLineSegment(sketch, "E809", {"start": v(9.59, -13.2) * mm, "end": v(9.63, -13.2) * mm});
            skLineSegment(sketch, "E810", {"start": v(9.63, -13.2) * mm, "end": v(9.7, -13.23) * mm});
            skLineSegment(sketch, "E811", {"start": v(9.7, -13.23) * mm, "end": v(9.84, -13.33) * mm});
            skLineSegment(sketch, "E812", {"start": v(9.84, -13.33) * mm, "end": v(10, -13.44) * mm});
            skLineSegment(sketch, "E813", {"start": v(10, -13.44) * mm, "end": v(10.2, -13.54) * mm});
            skLineSegment(sketch, "E814", {"start": v(10.2, -13.54) * mm, "end": v(10.41, -13.66) * mm});
            skLineSegment(sketch, "E815", {"start": v(10.41, -13.66) * mm, "end": v(10.67, -13.78) * mm});
            skLineSegment(sketch, "E816", {"start": v(10.67, -13.78) * mm, "end": v(10.93, -13.88) * mm});
            skLineSegment(sketch, "E817", {"start": v(10.93, -13.88) * mm, "end": v(11.14, -13.7) * mm});
            skLineSegment(sketch, "E818", {"start": v(11.14, -13.7) * mm, "end": v(11.34, -13.47) * mm});
            skLineSegment(sketch, "E819", {"start": v(11.34, -13.47) * mm, "end": v(11.23, -13.21) * mm});
            skLineSegment(sketch, "E820", {"start": v(11.23, -13.21) * mm, "end": v(11.11, -12.96) * mm});
            skLineSegment(sketch, "E821", {"start": v(11.11, -12.96) * mm, "end": v(11, -12.74) * mm});
            skLineSegment(sketch, "E822", {"start": v(11, -12.74) * mm, "end": v(10.89, -12.55) * mm});
            skLineSegment(sketch, "E823", {"start": v(10.89, -12.55) * mm, "end": v(10.79, -12.4) * mm});
            skLineSegment(sketch, "E824", {"start": v(10.79, -12.4) * mm, "end": v(10.68, -12.24) * mm});
            skLineSegment(sketch, "E825", {"start": v(10.68, -12.24) * mm, "end": v(10.65, -12.18) * mm});
            skLineSegment(sketch, "E826", {"start": v(10.65, -12.18) * mm, "end": v(10.65, -12.13) * mm});
            skLineSegment(sketch, "E827", {"start": v(10.65, -12.13) * mm, "end": v(11.07, -11.66) * mm});
            skLineSegment(sketch, "E828", {"start": v(11.07, -11.66) * mm, "end": v(11.11, -11.65) * mm});
            skLineSegment(sketch, "E829", {"start": v(11.11, -11.65) * mm, "end": v(11.18, -11.67) * mm});
            skLineSegment(sketch, "E830", {"start": v(11.18, -11.67) * mm, "end": v(11.34, -11.76) * mm});
            skLineSegment(sketch, "E831", {"start": v(11.34, -11.76) * mm, "end": v(11.51, -11.84) * mm});
            skLineSegment(sketch, "E832", {"start": v(11.51, -11.84) * mm, "end": v(11.71, -11.92) * mm});
            skLineSegment(sketch, "E833", {"start": v(11.71, -11.92) * mm, "end": v(11.95, -12) * mm});
            skLineSegment(sketch, "E834", {"start": v(11.95, -12) * mm, "end": v(12.21, -12.09) * mm});
            skLineSegment(sketch, "E835", {"start": v(12.21, -12.09) * mm, "end": v(12.49, -12.16) * mm});
            skLineSegment(sketch, "E836", {"start": v(12.49, -12.16) * mm, "end": v(12.68, -11.94) * mm});
            skLineSegment(sketch, "E837", {"start": v(12.68, -11.94) * mm, "end": v(12.84, -11.7) * mm});
            skLineSegment(sketch, "E838", {"start": v(12.84, -11.7) * mm, "end": v(12.7, -11.46) * mm});
            skLineSegment(sketch, "E839", {"start": v(12.7, -11.46) * mm, "end": v(12.55, -11.22) * mm});
            skLineSegment(sketch, "E840", {"start": v(12.55, -11.22) * mm, "end": v(12.4, -11.02) * mm});
            skLineSegment(sketch, "E841", {"start": v(12.4, -11.02) * mm, "end": v(12.28, -10.84) * mm});
            skLineSegment(sketch, "E842", {"start": v(12.28, -10.84) * mm, "end": v(12.16, -10.7) * mm});
            skLineSegment(sketch, "E843", {"start": v(12.16, -10.7) * mm, "end": v(12.03, -10.56) * mm});
            skLineSegment(sketch, "E844", {"start": v(12.03, -10.56) * mm, "end": v(12, -10.5) * mm});
            skLineSegment(sketch, "E845", {"start": v(12, -10.5) * mm, "end": v(11.98, -10.46) * mm});
            skLineSegment(sketch, "E846", {"start": v(11.98, -10.46) * mm, "end": v(12.34, -9.93) * mm});
            skLineSegment(sketch, "E847", {"start": v(12.34, -9.93) * mm, "end": v(12.38, -9.92) * mm});
            skLineSegment(sketch, "E848", {"start": v(12.38, -9.92) * mm, "end": v(12.45, -9.94) * mm});
            skLineSegment(sketch, "E849", {"start": v(12.45, -9.94) * mm, "end": v(12.62, -10) * mm});
            skLineSegment(sketch, "E850", {"start": v(12.62, -10) * mm, "end": v(12.8, -10.06) * mm});
            skLineSegment(sketch, "E851", {"start": v(12.8, -10.06) * mm, "end": v(13.01, -10.11) * mm});
            skLineSegment(sketch, "E852", {"start": v(13.01, -10.11) * mm, "end": v(13.25, -10.17) * mm});
            skLineSegment(sketch, "E853", {"start": v(13.25, -10.17) * mm, "end": v(13.53, -10.21) * mm});
            skLineSegment(sketch, "E854", {"start": v(13.53, -10.21) * mm, "end": v(13.8, -10.25) * mm});
            skLineSegment(sketch, "E855", {"start": v(13.8, -10.25) * mm, "end": v(13.97, -10) * mm});
            skLineSegment(sketch, "E856", {"start": v(13.97, -10) * mm, "end": v(14.1, -9.75) * mm});
            skLineSegment(sketch, "E857", {"start": v(14.1, -9.75) * mm, "end": v(13.93, -9.52) * mm});
            skLineSegment(sketch, "E858", {"start": v(13.93, -9.52) * mm, "end": v(13.75, -9.3) * mm});
            skLineSegment(sketch, "E859", {"start": v(13.75, -9.3) * mm, "end": v(13.58, -9.13) * mm});
            skLineSegment(sketch, "E860", {"start": v(13.58, -9.13) * mm, "end": v(13.43, -8.97) * mm});
            skLineSegment(sketch, "E861", {"start": v(13.43, -8.97) * mm, "end": v(13.29, -8.84) * mm});
            skLineSegment(sketch, "E862", {"start": v(13.29, -8.84) * mm, "end": v(13.15, -8.73) * mm});
            skLineSegment(sketch, "E863", {"start": v(13.15, -8.73) * mm, "end": v(13.1, -8.67) * mm});
            skLineSegment(sketch, "E864", {"start": v(13.1, -8.67) * mm, "end": v(13.09, -8.63) * mm});
            skLineSegment(sketch, "E865", {"start": v(13.09, -8.63) * mm, "end": v(13.37, -8.06) * mm});
            skLineSegment(sketch, "E866", {"start": v(13.37, -8.06) * mm, "end": v(13.41, -8.05) * mm});
            skLineSegment(sketch, "E867", {"start": v(13.41, -8.05) * mm, "end": v(13.48, -8.05) * mm});
            skLineSegment(sketch, "E868", {"start": v(13.48, -8.05) * mm, "end": v(13.66, -8.1) * mm});
            skLineSegment(sketch, "E869", {"start": v(13.66, -8.1) * mm, "end": v(13.85, -8.12) * mm});
            skLineSegment(sketch, "E870", {"start": v(13.85, -8.12) * mm, "end": v(14.06, -8.15) * mm});
            skLineSegment(sketch, "E871", {"start": v(14.06, -8.15) * mm, "end": v(14.3, -8.17) * mm});
            skLineSegment(sketch, "E872", {"start": v(14.3, -8.17) * mm, "end": v(14.59, -8.18) * mm});
            skLineSegment(sketch, "E873", {"start": v(14.59, -8.18) * mm, "end": v(14.87, -8.18) * mm});
            skLineSegment(sketch, "E874", {"start": v(14.87, -8.18) * mm, "end": v(15, -7.92) * mm});
            skLineSegment(sketch, "E875", {"start": v(15, -7.92) * mm, "end": v(15.1, -7.65) * mm});
            skLineSegment(sketch, "E876", {"start": v(15.1, -7.65) * mm, "end": v(14.9, -7.45) * mm});
            skLineSegment(sketch, "E877", {"start": v(14.9, -7.45) * mm, "end": v(14.69, -7.26) * mm});
            skLineSegment(sketch, "E878", {"start": v(14.69, -7.26) * mm, "end": v(14.5, -7.1) * mm});
            skLineSegment(sketch, "E879", {"start": v(14.5, -7.1) * mm, "end": v(14.33, -6.97) * mm});
            skLineSegment(sketch, "E880", {"start": v(14.33, -6.97) * mm, "end": v(14.17, -6.86) * mm});
            skLineSegment(sketch, "E881", {"start": v(14.17, -6.86) * mm, "end": v(14.02, -6.76) * mm});
            skLineSegment(sketch, "E882", {"start": v(14.02, -6.76) * mm, "end": v(13.96, -6.71) * mm});
            skLineSegment(sketch, "E883", {"start": v(13.96, -6.71) * mm, "end": v(13.95, -6.67) * mm});
            skLineSegment(sketch, "E884", {"start": v(13.95, -6.67) * mm, "end": v(14.15, -6.07) * mm});
            skLineSegment(sketch, "E885", {"start": v(14.15, -6.07) * mm, "end": v(14.19, -6.05) * mm});
            skLineSegment(sketch, "E886", {"start": v(14.19, -6.05) * mm, "end": v(14.26, -6.05) * mm});
            skLineSegment(sketch, "E887", {"start": v(14.26, -6.05) * mm, "end": v(14.44, -6.06) * mm});
            skLineSegment(sketch, "E888", {"start": v(14.44, -6.06) * mm, "end": v(14.63, -6.07) * mm});
            skLineSegment(sketch, "E889", {"start": v(14.63, -6.07) * mm, "end": v(14.85, -6.07) * mm});
            skLineSegment(sketch, "E890", {"start": v(14.85, -6.07) * mm, "end": v(15.1, -6.06) * mm});
            skLineSegment(sketch, "E891", {"start": v(15.1, -6.06) * mm, "end": v(15.37, -6.03) * mm});
            skLineSegment(sketch, "E892", {"start": v(15.37, -6.03) * mm, "end": v(15.65, -6) * mm});
            skLineSegment(sketch, "E893", {"start": v(15.65, -6) * mm, "end": v(15.75, -5.72) * mm});
            skLineSegment(sketch, "E894", {"start": v(15.75, -5.72) * mm, "end": v(15.8, -5.43) * mm});
            skLineSegment(sketch, "E895", {"start": v(15.8, -5.43) * mm, "end": v(15.58, -5.26) * mm});
            skLineSegment(sketch, "E896", {"start": v(15.58, -5.26) * mm, "end": v(15.35, -5.1) * mm});
            skLineSegment(sketch, "E897", {"start": v(15.35, -5.1) * mm, "end": v(15.14, -4.97) * mm});
            skLineSegment(sketch, "E898", {"start": v(15.14, -4.97) * mm, "end": v(14.95, -4.86) * mm});
            skLineSegment(sketch, "E899", {"start": v(14.95, -4.86) * mm, "end": v(14.79, -4.77) * mm});
            skLineSegment(sketch, "E900", {"start": v(14.79, -4.77) * mm, "end": v(14.62, -4.7) * mm});
            skLineSegment(sketch, "E901", {"start": v(14.62, -4.7) * mm, "end": v(14.56, -4.65) * mm});
            skLineSegment(sketch, "E902", {"start": v(14.56, -4.65) * mm, "end": v(14.54, -4.62) * mm});
            skLineSegment(sketch, "E903", {"start": v(14.54, -4.62) * mm, "end": v(14.66, -4) * mm});
            skLineSegment(sketch, "E904", {"start": v(14.66, -4) * mm, "end": v(14.7, -3.97) * mm});
            skLineSegment(sketch, "E905", {"start": v(14.7, -3.97) * mm, "end": v(14.77, -3.96) * mm});
            skLineSegment(sketch, "E906", {"start": v(14.77, -3.96) * mm, "end": v(14.95, -3.95) * mm});
            skLineSegment(sketch, "E907", {"start": v(14.95, -3.95) * mm, "end": v(15.14, -3.93) * mm});
            skLineSegment(sketch, "E908", {"start": v(15.14, -3.93) * mm, "end": v(15.35, -3.9) * mm});
            skLineSegment(sketch, "E909", {"start": v(15.35, -3.9) * mm, "end": v(15.6, -3.86) * mm});
            skLineSegment(sketch, "E910", {"start": v(15.6, -3.86) * mm, "end": v(15.87, -3.8) * mm});
            skLineSegment(sketch, "E911", {"start": v(15.87, -3.8) * mm, "end": v(16.14, -3.72) * mm});
            skLineSegment(sketch, "E912", {"start": v(-0.9, -3.58) * mm, "end": v(-1.43, -3.63) * mm});
            skLineSegment(sketch, "E913", {"start": v(-1.43, -3.63) * mm, "end": v(-1.95, -3.58) * mm});
            skLineSegment(sketch, "E914", {"start": v(-1.95, -3.58) * mm, "end": v(-2.45, -3.41) * mm});
            skLineSegment(sketch, "E915", {"start": v(-2.45, -3.41) * mm, "end": v(-2.9, -3.15) * mm});
            skLineSegment(sketch, "E916", {"start": v(-2.9, -3.15) * mm, "end": v(-3.3, -2.8) * mm});
            skLineSegment(sketch, "E917", {"start": v(-3.3, -2.8) * mm, "end": v(-3.6, -2.37) * mm});
            skLineSegment(sketch, "E918", {"start": v(-3.6, -2.37) * mm, "end": v(-3.82, -1.9) * mm});
            skLineSegment(sketch, "E919", {"start": v(-3.82, -1.9) * mm, "end": v(-3.93, -1.38) * mm});
            skLineSegment(sketch, "E920", {"start": v(-3.93, -1.38) * mm, "end": v(-3.93, -0.85) * mm});
            skLineSegment(sketch, "E921", {"start": v(-3.93, -0.85) * mm, "end": v(-3.82, -0.34) * mm});
            skLineSegment(sketch, "E922", {"start": v(-3.82, -0.34) * mm, "end": v(-3.6, 0.14) * mm});
            skLineSegment(sketch, "E923", {"start": v(-3.6, 0.14) * mm, "end": v(-3.3, 0.56) * mm});
            skLineSegment(sketch, "E924", {"start": v(-3.3, 0.56) * mm, "end": v(-2.96, 0.87) * mm});
            skLineSegment(sketch, "E925", {"start": v(0.1, 0.87) * mm, "end": v(0.44, 0.56) * mm});
            skLineSegment(sketch, "E926", {"start": v(0.44, 0.56) * mm, "end": v(0.75, 0.14) * mm});
            skLineSegment(sketch, "E927", {"start": v(0.75, 0.14) * mm, "end": v(0.96, -0.34) * mm});
            skLineSegment(sketch, "E928", {"start": v(0.96, -0.34) * mm, "end": v(1.07, -0.85) * mm});
            skLineSegment(sketch, "E929", {"start": v(1.07, -0.85) * mm, "end": v(1.07, -1.38) * mm});
            skLineSegment(sketch, "E930", {"start": v(1.07, -1.38) * mm, "end": v(0.96, -1.9) * mm});
            skLineSegment(sketch, "E931", {"start": v(0.96, -1.9) * mm, "end": v(0.75, -2.37) * mm});
            skLineSegment(sketch, "E932", {"start": v(0.75, -2.37) * mm, "end": v(0.44, -2.8) * mm});
            skLineSegment(sketch, "E933", {"start": v(0.44, -2.8) * mm, "end": v(0.05, -3.15) * mm});
            skLineSegment(sketch, "E934", {"start": v(0.05, -3.15) * mm, "end": v(-0.4, -3.41) * mm});
            skLineSegment(sketch, "E935", {"start": v(-0.4, -3.41) * mm, "end": v(-0.9, -3.58) * mm});
            skLineSegment(sketch, "E936", {"start": v(16.37, 45.5) * mm, "end": v(14.93, 45) * mm});
            skLineSegment(sketch, "E937", {"start": v(14.93, 45) * mm, "end": v(14.93, 44.38) * mm});
            skLineSegment(sketch, "E938", {"start": v(14.93, 44.38) * mm, "end": v(16.37, 43.89) * mm});
            skLineSegment(sketch, "E939", {"start": v(16.37, 43.89) * mm, "end": v(16.37, 43.26) * mm});
            skLineSegment(sketch, "E940", {"start": v(16.37, 43.26) * mm, "end": v(14.93, 42.77) * mm});
            skLineSegment(sketch, "E941", {"start": v(14.93, 42.77) * mm, "end": v(14.93, 42.14) * mm});
            skLineSegment(sketch, "E942", {"start": v(14.93, 42.14) * mm, "end": v(16.37, 41.65) * mm});
            skLineSegment(sketch, "E943", {"start": v(16.37, 41.65) * mm, "end": v(16.37, 41.02) * mm});
            skLineSegment(sketch, "E944", {"start": v(16.37, 41.02) * mm, "end": v(14.93, 40.53) * mm});
            skLineSegment(sketch, "E945", {"start": v(14.93, 40.53) * mm, "end": v(14.93, 39.9) * mm});
            skLineSegment(sketch, "E946", {"start": v(14.93, 39.9) * mm, "end": v(16.37, 39.42) * mm});
            skLineSegment(sketch, "E947", {"start": v(16.37, 39.42) * mm, "end": v(16.37, 38.79) * mm});
            skLineSegment(sketch, "E948", {"start": v(16.37, 38.79) * mm, "end": v(14.93, 38.3) * mm});
            skLineSegment(sketch, "E949", {"start": v(14.93, 38.3) * mm, "end": v(14.93, 37.67) * mm});
            skLineSegment(sketch, "E950", {"start": v(14.93, 37.67) * mm, "end": v(16.37, 37.18) * mm});
            skLineSegment(sketch, "E951", {"start": v(16.37, 37.18) * mm, "end": v(16.37, 36.55) * mm});
            skLineSegment(sketch, "E952", {"start": v(16.37, 36.55) * mm, "end": v(14.93, 36.06) * mm});
            skLineSegment(sketch, "E953", {"start": v(14.93, 36.06) * mm, "end": v(14.93, 35.44) * mm});
            skLineSegment(sketch, "E954", {"start": v(14.93, 35.44) * mm, "end": v(16.37, 34.95) * mm});
            skLineSegment(sketch, "E955", {"start": v(16.37, 34.95) * mm, "end": v(16.37, 34.32) * mm});
            skLineSegment(sketch, "E956", {"start": v(16.37, 34.32) * mm, "end": v(14.93, 33.83) * mm});
            skLineSegment(sketch, "E957", {"start": v(14.93, 33.83) * mm, "end": v(14.93, 33.2) * mm});
            skLineSegment(sketch, "E958", {"start": v(14.93, 33.2) * mm, "end": v(16.37, 32.71) * mm});
            skLineSegment(sketch, "E959", {"start": v(16.37, 32.71) * mm, "end": v(16.37, 32.09) * mm});
            skLineSegment(sketch, "E960", {"start": v(16.37, 32.09) * mm, "end": v(14.93, 31.6) * mm});
            skLineSegment(sketch, "E961", {"start": v(14.93, 31.6) * mm, "end": v(14.93, 30.97) * mm});
            skLineSegment(sketch, "E962", {"start": v(14.93, 30.97) * mm, "end": v(16.37, 30.48) * mm});
            skLineSegment(sketch, "E963", {"start": v(16.37, 30.48) * mm, "end": v(16.37, 29.85) * mm});
            skLineSegment(sketch, "E964", {"start": v(16.37, 29.85) * mm, "end": v(14.93, 29.36) * mm});
            skLineSegment(sketch, "E965", {"start": v(14.93, 29.36) * mm, "end": v(14.93, 28.74) * mm});
            skLineSegment(sketch, "E966", {"start": v(14.93, 28.74) * mm, "end": v(16.37, 28.25) * mm});
            skLineSegment(sketch, "E967", {"start": v(16.37, 28.25) * mm, "end": v(16.37, 27.62) * mm});
            skLineSegment(sketch, "E968", {"start": v(16.37, 27.62) * mm, "end": v(14.93, 27.13) * mm});
            skLineSegment(sketch, "E969", {"start": v(14.93, 27.13) * mm, "end": v(14.93, 26.5) * mm});
            skLineSegment(sketch, "E970", {"start": v(14.93, 26.5) * mm, "end": v(16.37, 26.01) * mm});
            skLineSegment(sketch, "E971", {"start": v(16.37, 26.01) * mm, "end": v(16.37, 25.38) * mm});
            skLineSegment(sketch, "E972", {"start": v(16.37, 25.38) * mm, "end": v(14.93, 24.9) * mm});
            skLineSegment(sketch, "E973", {"start": v(14.93, 24.9) * mm, "end": v(14.93, 24.27) * mm});
            skLineSegment(sketch, "E974", {"start": v(14.93, 24.27) * mm, "end": v(16.37, 23.78) * mm});
            skLineSegment(sketch, "E975", {"start": v(16.37, 23.78) * mm, "end": v(16.37, 23.15) * mm});
            skLineSegment(sketch, "E976", {"start": v(16.37, 23.15) * mm, "end": v(14.93, 22.66) * mm});
            skLineSegment(sketch, "E977", {"start": v(14.93, 22.66) * mm, "end": v(14.93, 22.03) * mm});
            skLineSegment(sketch, "E978", {"start": v(14.93, 22.03) * mm, "end": v(16.37, 21.54) * mm});
            skLineSegment(sketch, "E979", {"start": v(16.37, 21.54) * mm, "end": v(16.37, 20.91) * mm});
            skLineSegment(sketch, "E980", {"start": v(16.37, 20.91) * mm, "end": v(14.93, 20.42) * mm});
            skLineSegment(sketch, "E981", {"start": v(14.93, 20.42) * mm, "end": v(14.93, 19.8) * mm});
            skLineSegment(sketch, "E982", {"start": v(14.93, 19.8) * mm, "end": v(16.37, 19.3) * mm});
            skLineSegment(sketch, "E983", {"start": v(16.37, 19.3) * mm, "end": v(16.37, 18.68) * mm});
            skLineSegment(sketch, "E984", {"start": v(16.37, 18.68) * mm, "end": v(14.93, 18.19) * mm});
            skLineSegment(sketch, "E985", {"start": v(14.93, 18.19) * mm, "end": v(14.93, 17.56) * mm});
            skLineSegment(sketch, "E986", {"start": v(14.93, 17.56) * mm, "end": v(16.37, 17.07) * mm});
            skLineSegment(sketch, "E987", {"start": v(16.37, 17.07) * mm, "end": v(16.37, 16.44) * mm});
            skLineSegment(sketch, "E988", {"start": v(16.37, 16.44) * mm, "end": v(14.93, 15.95) * mm});
            skLineSegment(sketch, "E989", {"start": v(14.93, 15.95) * mm, "end": v(14.93, 15.33) * mm});
            skLineSegment(sketch, "E990", {"start": v(14.93, 15.33) * mm, "end": v(16.37, 14.84) * mm});
            skLineSegment(sketch, "E991", {"start": v(16.37, 14.84) * mm, "end": v(16.37, 14.2) * mm});
            skLineSegment(sketch, "E992", {"start": v(16.37, 14.2) * mm, "end": v(14.93, 13.72) * mm});
            skLineSegment(sketch, "E993", {"start": v(14.93, 13.72) * mm, "end": v(14.93, 13.1) * mm});
            skLineSegment(sketch, "E994", {"start": v(14.93, 13.1) * mm, "end": v(16.37, 12.6) * mm});
            skLineSegment(sketch, "E995", {"start": v(16.37, 12.6) * mm, "end": v(16.37, 11.98) * mm});
            skLineSegment(sketch, "E996", {"start": v(16.37, 11.98) * mm, "end": v(14.93, 11.48) * mm});
            skLineSegment(sketch, "E997", {"start": v(14.93, 11.48) * mm, "end": v(14.93, 10.86) * mm});
            skLineSegment(sketch, "E998", {"start": v(14.93, 10.86) * mm, "end": v(16.37, 10.37) * mm});
            skLineSegment(sketch, "E999", {"start": v(16.37, 10.37) * mm, "end": v(16.37, 9.74) * mm});
            skLineSegment(sketch, "E1000", {"start": v(16.37, 9.74) * mm, "end": v(14.93, 9.25) * mm});
            skLineSegment(sketch, "E1001", {"start": v(14.93, 9.25) * mm, "end": v(14.93, 8.63) * mm});
            skLineSegment(sketch, "E1002", {"start": v(14.93, 8.63) * mm, "end": v(16.37, 8.13) * mm});
            skLineSegment(sketch, "E1003", {"start": v(16.37, 8.13) * mm, "end": v(16.37, 7.5) * mm});
            skLineSegment(sketch, "E1004", {"start": v(16.37, 7.5) * mm, "end": v(14.93, 7.02) * mm});
            skLineSegment(sketch, "E1005", {"start": v(14.93, 7.02) * mm, "end": v(14.93, 6.4) * mm});
            skLineSegment(sketch, "E1006", {"start": v(14.93, 6.4) * mm, "end": v(16.37, 5.9) * mm});
            skLineSegment(sketch, "E1007", {"start": v(16.37, 5.9) * mm, "end": v(16.37, 5.27) * mm});
            skLineSegment(sketch, "E1008", {"start": v(16.37, 5.27) * mm, "end": v(14.93, 4.78) * mm});
            skLineSegment(sketch, "E1009", {"start": v(14.93, 4.78) * mm, "end": v(14.93, 4.16) * mm});
            skLineSegment(sketch, "E1010", {"start": v(14.93, 4.16) * mm, "end": v(16.37, 3.67) * mm});
            skLineSegment(sketch, "E1011", {"start": v(16.37, 3.67) * mm, "end": v(16.37, 3.04) * mm});
            skLineSegment(sketch, "E1012", {"start": v(16.37, 3.04) * mm, "end": v(14.93, 2.55) * mm});
            skLineSegment(sketch, "E1013", {"start": v(14.93, 2.55) * mm, "end": v(14.93, 1.92) * mm});
            skLineSegment(sketch, "E1014", {"start": v(14.93, 1.92) * mm, "end": v(16.37, 1.43) * mm});
            skLineSegment(sketch, "E1015", {"start": v(16.37, 1.43) * mm, "end": v(16.37, 0.8) * mm});
            skLineSegment(sketch, "E1016", {"start": v(16.37, 0.8) * mm, "end": v(14.93, 0.31) * mm});
            skLineSegment(sketch, "E1017", {"start": v(14.93, 0.31) * mm, "end": v(14.93, -0.31) * mm});
            skLineSegment(sketch, "E1018", {"start": v(14.93, -0.31) * mm, "end": v(16.37, -0.8) * mm});
            skLineSegment(sketch, "E1019", {"start": v(16.37, -0.8) * mm, "end": v(16.37, -1.43) * mm});
            skLineSegment(sketch, "E1020", {"start": v(16.37, -1.43) * mm, "end": v(14.93, -1.92) * mm});
            skLineSegment(sketch, "E1021", {"start": v(14.93, -1.92) * mm, "end": v(14.93, -2.55) * mm});
            skLineSegment(sketch, "E1022", {"start": v(14.93, -2.55) * mm, "end": v(16.37, -3.04) * mm});
            skLineSegment(sketch, "E1023", {"start": v(16.37, -3.04) * mm, "end": v(16.37, -3.67) * mm});
            skLineSegment(sketch, "E1024", {"start": v(16.37, -3.67) * mm, "end": v(14.93, -4.16) * mm});
            skLineSegment(sketch, "E1025", {"start": v(14.93, -4.16) * mm, "end": v(14.93, -4.78) * mm});
            skLineSegment(sketch, "E1026", {"start": v(14.93, -4.78) * mm, "end": v(16.37, -5.27) * mm});
            skLineSegment(sketch, "E1027", {"start": v(16.37, -5.27) * mm, "end": v(16.37, -5.9) * mm});
            skLineSegment(sketch, "E1028", {"start": v(16.37, -5.9) * mm, "end": v(14.93, -6.4) * mm});
            skLineSegment(sketch, "E1029", {"start": v(14.93, -6.4) * mm, "end": v(14.93, -7.02) * mm});
            skLineSegment(sketch, "E1030", {"start": v(14.93, -7.02) * mm, "end": v(16.37, -7.5) * mm});
            skLineSegment(sketch, "E1031", {"start": v(16.37, -7.5) * mm, "end": v(16.37, -8.13) * mm});
            skLineSegment(sketch, "E1032", {"start": v(16.37, -8.13) * mm, "end": v(14.93, -8.63) * mm});
            skLineSegment(sketch, "E1033", {"start": v(14.93, -8.63) * mm, "end": v(14.93, -9.25) * mm});
            skLineSegment(sketch, "E1034", {"start": v(14.93, -9.25) * mm, "end": v(16.37, -9.74) * mm});
            skLineSegment(sketch, "E1035", {"start": v(16.37, -9.74) * mm, "end": v(16.37, -10.37) * mm});
            skLineSegment(sketch, "E1036", {"start": v(16.37, -10.37) * mm, "end": v(14.93, -10.86) * mm});
            skLineSegment(sketch, "E1037", {"start": v(14.93, -10.86) * mm, "end": v(14.93, -11.48) * mm});
            skLineSegment(sketch, "E1038", {"start": v(14.93, -11.48) * mm, "end": v(16.37, -11.98) * mm});
            skLineSegment(sketch, "E1039", {"start": v(16.37, -11.98) * mm, "end": v(16.37, -12.6) * mm});
            skLineSegment(sketch, "E1040", {"start": v(16.37, -12.6) * mm, "end": v(14.93, -13.1) * mm});
            skLineSegment(sketch, "E1041", {"start": v(14.93, -13.1) * mm, "end": v(14.93, -13.72) * mm});
            skLineSegment(sketch, "E1042", {"start": v(14.93, -13.72) * mm, "end": v(16.37, -14.2) * mm});
            skLineSegment(sketch, "E1043", {"start": v(16.37, -14.2) * mm, "end": v(16.37, -14.84) * mm});
            skLineSegment(sketch, "E1044", {"start": v(16.37, -14.84) * mm, "end": v(14.93, -15.33) * mm});
            skLineSegment(sketch, "E1045", {"start": v(14.93, -15.33) * mm, "end": v(14.93, -15.95) * mm});
            skLineSegment(sketch, "E1046", {"start": v(14.93, -15.95) * mm, "end": v(16.37, -16.44) * mm});
            skLineSegment(sketch, "E1047", {"start": v(16.37, -16.44) * mm, "end": v(16.37, -17.07) * mm});
            skLineSegment(sketch, "E1048", {"start": v(16.37, -17.07) * mm, "end": v(14.93, -17.56) * mm});
            skLineSegment(sketch, "E1049", {"start": v(14.93, -17.56) * mm, "end": v(14.93, -18.19) * mm});
            skLineSegment(sketch, "E1050", {"start": v(14.93, -18.19) * mm, "end": v(16.37, -18.68) * mm});
            skLineSegment(sketch, "E1051", {"start": v(16.37, -18.68) * mm, "end": v(16.37, -19.3) * mm});
            skLineSegment(sketch, "E1052", {"start": v(16.37, -19.3) * mm, "end": v(14.93, -19.8) * mm});
            skLineSegment(sketch, "E1053", {"start": v(14.93, -19.8) * mm, "end": v(14.93, -20.42) * mm});
            skLineSegment(sketch, "E1054", {"start": v(14.93, -20.42) * mm, "end": v(16.37, -20.91) * mm});
            skLineSegment(sketch, "E1055", {"start": v(16.37, -20.91) * mm, "end": v(16.37, -21.54) * mm});
            skLineSegment(sketch, "E1056", {"start": v(16.37, -21.54) * mm, "end": v(14.93, -22.03) * mm});
            skLineSegment(sketch, "E1057", {"start": v(14.93, -22.03) * mm, "end": v(14.93, -22.66) * mm});
            skLineSegment(sketch, "E1058", {"start": v(14.93, -22.66) * mm, "end": v(16.37, -23.15) * mm});
            skLineSegment(sketch, "E1059", {"start": v(16.37, -23.15) * mm, "end": v(16.37, -23.78) * mm});
            skLineSegment(sketch, "E1060", {"start": v(16.37, -23.78) * mm, "end": v(14.93, -24.27) * mm});
            skLineSegment(sketch, "E1061", {"start": v(14.93, -24.27) * mm, "end": v(14.93, -24.9) * mm});
            skLineSegment(sketch, "E1062", {"start": v(14.93, -24.9) * mm, "end": v(16.37, -25.38) * mm});
            skLineSegment(sketch, "E1063", {"start": v(16.37, -25.38) * mm, "end": v(16.37, -26.01) * mm});
            skLineSegment(sketch, "E1064", {"start": v(16.37, -26.01) * mm, "end": v(14.93, -26.5) * mm});
            skLineSegment(sketch, "E1065", {"start": v(14.93, -26.5) * mm, "end": v(14.93, -27.13) * mm});
            skLineSegment(sketch, "E1066", {"start": v(14.93, -27.13) * mm, "end": v(16.37, -27.62) * mm});
            skLineSegment(sketch, "E1067", {"start": v(16.37, -27.62) * mm, "end": v(16.37, -28.25) * mm});
            skLineSegment(sketch, "E1068", {"start": v(16.37, -28.25) * mm, "end": v(14.93, -28.74) * mm});
            skLineSegment(sketch, "E1069", {"start": v(14.93, -28.74) * mm, "end": v(14.93, -29.36) * mm});
            skLineSegment(sketch, "E1070", {"start": v(14.93, -29.36) * mm, "end": v(16.37, -29.85) * mm});
            skLineSegment(sketch, "E1071", {"start": v(16.37, -29.85) * mm, "end": v(16.37, -30.48) * mm});
            skLineSegment(sketch, "E1072", {"start": v(16.37, -30.48) * mm, "end": v(14.93, -30.97) * mm});
            skLineSegment(sketch, "E1073", {"start": v(14.93, -30.97) * mm, "end": v(14.93, -31.6) * mm});
            skLineSegment(sketch, "E1074", {"start": v(14.93, -31.6) * mm, "end": v(16.37, -32.09) * mm});
            skLineSegment(sketch, "E1075", {"start": v(16.37, -32.09) * mm, "end": v(16.37, -32.71) * mm});
            skLineSegment(sketch, "E1076", {"start": v(16.37, -32.71) * mm, "end": v(14.93, -33.2) * mm});
            skLineSegment(sketch, "E1077", {"start": v(14.93, -33.2) * mm, "end": v(14.93, -33.83) * mm});
            skLineSegment(sketch, "E1078", {"start": v(14.93, -33.83) * mm, "end": v(16.37, -34.32) * mm});
            skLineSegment(sketch, "E1079", {"start": v(16.37, -34.32) * mm, "end": v(16.37, -34.95) * mm});
            skLineSegment(sketch, "E1080", {"start": v(16.37, -34.95) * mm, "end": v(14.93, -35.44) * mm});
            skLineSegment(sketch, "E1081", {"start": v(14.93, -35.44) * mm, "end": v(14.93, -36.06) * mm});
            skLineSegment(sketch, "E1082", {"start": v(14.93, -36.06) * mm, "end": v(16.37, -36.55) * mm});
            skLineSegment(sketch, "E1083", {"start": v(16.37, -36.55) * mm, "end": v(16.37, -37.18) * mm});
            skLineSegment(sketch, "E1084", {"start": v(16.37, -37.18) * mm, "end": v(14.93, -37.67) * mm});
            skLineSegment(sketch, "E1085", {"start": v(14.93, -37.67) * mm, "end": v(14.93, -38.3) * mm});
            skLineSegment(sketch, "E1086", {"start": v(14.93, -38.3) * mm, "end": v(16.37, -38.79) * mm});
            skLineSegment(sketch, "E1087", {"start": v(16.37, -38.79) * mm, "end": v(16.37, -39.42) * mm});
            skLineSegment(sketch, "E1088", {"start": v(16.37, -39.42) * mm, "end": v(14.93, -39.9) * mm});
            skLineSegment(sketch, "E1089", {"start": v(14.93, -39.9) * mm, "end": v(14.93, -40.53) * mm});
            skLineSegment(sketch, "E1090", {"start": v(14.93, -40.53) * mm, "end": v(16.37, -41.02) * mm});
            skLineSegment(sketch, "E1091", {"start": v(16.37, -41.02) * mm, "end": v(16.37, -41.65) * mm});
            skLineSegment(sketch, "E1092", {"start": v(16.37, -41.65) * mm, "end": v(14.93, -42.14) * mm});
            skLineSegment(sketch, "E1093", {"start": v(14.93, -42.14) * mm, "end": v(14.93, -42.77) * mm});
            skLineSegment(sketch, "E1094", {"start": v(14.93, -42.77) * mm, "end": v(16.37, -43.26) * mm});
            skLineSegment(sketch, "E1095", {"start": v(16.37, -43.26) * mm, "end": v(16.37, -43.89) * mm});
            skLineSegment(sketch, "E1096", {"start": v(16.37, -43.89) * mm, "end": v(14.93, -44.38) * mm});
            skLineSegment(sketch, "E1097", {"start": v(14.93, -44.38) * mm, "end": v(14.93, -45) * mm});
            skLineSegment(sketch, "E1098", {"start": v(14.93, -45) * mm, "end": v(16.37, -45.5) * mm});
            skLineSegment(sketch, "E1099", {"start": v(17.87, -45.8) * mm, "end": v(17.87, 45.8) * mm});
            skLineSegment(sketch, "E1100", {"start": v(17.87, 45.8) * mm, "end": v(16.37, 45.8) * mm});
            skLineSegment(sketch, "E1101", {"start": v(16.37, 45.8) * mm, "end": v(16.37, 45.5) * mm});
            skPoint(sketch, "E1102.endSnap0", {"position": v(-3.1, 0.74) * mm});
            skLineSegment(sketch, "E1103", {"start": v(-2.96, 0.87) * mm, "end": v(0.1, 0.87) * mm});
            skPoint(sketch, "E1104.orphan", {"position": v(-2.9, 0.92) * mm});
            skLineSegment(sketch, "E1105.0.1.0", {"start": v(14.93, -65.06) * mm, "end": v(16.37, -65.55) * mm});
            skLineSegment(sketch, "E1105.0.1.1", {"start": v(16.37, -52.15) * mm, "end": v(16.37, -52.78) * mm});
            skLineSegment(sketch, "E1105.0.1.2", {"start": v(14.93, -74) * mm, "end": v(16.37, -74.5) * mm});
            skLineSegment(sketch, "E1105.0.1.3", {"start": v(14.93, -47.19) * mm, "end": v(16.37, -47.68) * mm});
            skLineSegment(sketch, "E1105.0.1.4", {"start": v(14.93, -71.77) * mm, "end": v(16.37, -72.26) * mm});
            skLineSegment(sketch, "E1105.0.1.5", {"start": v(14.93, -53.9) * mm, "end": v(16.37, -54.38) * mm});
            skLineSegment(sketch, "E1105.0.1.6", {"start": v(14.93, -64.44) * mm, "end": v(14.93, -65.06) * mm});
            skLineSegment(sketch, "E1105.0.1.7", {"start": v(14.93, -73.38) * mm, "end": v(14.93, -74) * mm});
            skLineSegment(sketch, "E1105.0.1.8", {"start": v(16.37, -46.07) * mm, "end": v(14.93, -46.56) * mm});
            skLineSegment(sketch, "E1105.0.1.9", {"start": v(14.93, -58.36) * mm, "end": v(16.37, -58.85) * mm});
            skLineSegment(sketch, "E1105.0.1.10", {"start": v(14.93, -59.97) * mm, "end": v(14.93, -60.6) * mm});
            skLineSegment(sketch, "E1105.0.1.11", {"start": v(16.37, -63.95) * mm, "end": v(14.93, -64.44) * mm});
            skLineSegment(sketch, "E1105.0.1.12", {"start": v(16.37, -55.01) * mm, "end": v(14.93, -55.5) * mm});
            skLineSegment(sketch, "E1105.0.1.13", {"start": v(16.37, -72.89) * mm, "end": v(14.93, -73.38) * mm});
            skLineSegment(sketch, "E1105.0.1.14", {"start": v(14.93, -71.14) * mm, "end": v(14.93, -71.77) * mm});
            skLineSegment(sketch, "E1105.0.1.15", {"start": v(16.37, -66.18) * mm, "end": v(14.93, -66.67) * mm});
            skLineSegment(sketch, "E1105.0.1.16", {"start": v(14.93, -53.27) * mm, "end": v(14.93, -53.9) * mm});
            skLineSegment(sketch, "E1105.0.1.18", {"start": v(16.37, -48.3) * mm, "end": v(14.93, -48.8) * mm});
            skLineSegment(sketch, "E1105.0.1.19", {"start": v(16.37, -59.48) * mm, "end": v(14.93, -59.97) * mm});
            skLineSegment(sketch, "E1105.0.1.20", {"start": v(16.37, -72.26) * mm, "end": v(16.37, -72.89) * mm});
            skLineSegment(sketch, "E1105.0.1.21", {"start": v(14.93, -60.6) * mm, "end": v(16.37, -61.09) * mm});
            skLineSegment(sketch, "E1105.0.1.22", {"start": v(16.37, -58.85) * mm, "end": v(16.37, -59.48) * mm});
            skLineSegment(sketch, "E1105.0.1.23", {"start": v(14.93, -51.66) * mm, "end": v(16.37, -52.15) * mm});
            skLineSegment(sketch, "E1105.0.1.24", {"start": v(14.93, -46.56) * mm, "end": v(14.93, -47.19) * mm});
            skLineSegment(sketch, "E1105.0.1.25", {"start": v(16.37, -70.65) * mm, "end": v(14.93, -71.14) * mm});
            skLineSegment(sketch, "E1105.0.1.26", {"start": v(16.37, -61.71) * mm, "end": v(14.93, -62.2) * mm});
            skLineSegment(sketch, "E1105.0.1.27", {"start": v(16.37, -65.55) * mm, "end": v(16.37, -66.18) * mm});
            skLineSegment(sketch, "E1105.0.1.28", {"start": v(16.37, -52.78) * mm, "end": v(14.93, -53.27) * mm});
            skLineSegment(sketch, "E1105.0.1.30", {"start": v(16.37, -70.02) * mm, "end": v(16.37, -70.65) * mm});
            skLineSegment(sketch, "E1105.0.1.31", {"start": v(16.37, -61.09) * mm, "end": v(16.37, -61.71) * mm});
            skLineSegment(sketch, "E1105.0.1.32", {"start": v(14.93, -56.13) * mm, "end": v(16.37, -56.62) * mm});
            skLineSegment(sketch, "E1105.0.1.33", {"start": v(14.93, -62.83) * mm, "end": v(16.37, -63.32) * mm});
            skLineSegment(sketch, "E1105.0.1.34", {"start": v(16.37, -67.79) * mm, "end": v(16.37, -68.42) * mm});
            skLineSegment(sketch, "E1105.0.1.35", {"start": v(14.93, -55.5) * mm, "end": v(14.93, -56.13) * mm});
            skLineSegment(sketch, "E1105.0.1.36", {"start": v(16.37, -49.91) * mm, "end": v(16.37, -50.54) * mm});
            skLineSegment(sketch, "E1105.0.1.37", {"start": v(14.93, -67.3) * mm, "end": v(16.37, -67.79) * mm});
            skLineSegment(sketch, "E1105.0.1.38", {"start": v(14.93, -68.9) * mm, "end": v(14.93, -69.53) * mm});
            skLineSegment(sketch, "E1105.0.1.39", {"start": v(14.93, -49.42) * mm, "end": v(16.37, -49.91) * mm});
            skLineSegment(sketch, "E1105.0.1.40", {"start": v(14.93, -51.03) * mm, "end": v(14.93, -51.66) * mm});
            skLineSegment(sketch, "E1105.0.1.41", {"start": v(16.37, -57.25) * mm, "end": v(14.93, -57.74) * mm});
            skLineSegment(sketch, "E1105.0.1.42", {"start": v(16.37, -68.42) * mm, "end": v(14.93, -68.9) * mm});
            skLineSegment(sketch, "E1105.0.1.43", {"start": v(16.37, -63.32) * mm, "end": v(16.37, -63.95) * mm});
            skLineSegment(sketch, "E1105.0.1.44", {"start": v(16.37, -54.38) * mm, "end": v(16.37, -55.01) * mm});
            skLineSegment(sketch, "E1105.0.1.45", {"start": v(16.37, -50.54) * mm, "end": v(14.93, -51.03) * mm});
            skLineSegment(sketch, "E1105.0.1.46", {"start": v(14.93, -69.53) * mm, "end": v(16.37, -70.02) * mm});
            skLineSegment(sketch, "E1105.0.1.47", {"start": v(16.37, -56.62) * mm, "end": v(16.37, -57.25) * mm});
            skLineSegment(sketch, "E1105.0.1.48", {"start": v(14.93, -48.8) * mm, "end": v(14.93, -49.42) * mm});
            skLineSegment(sketch, "E1105.0.1.49", {"start": v(16.37, -47.68) * mm, "end": v(16.37, -48.3) * mm});
            skLineSegment(sketch, "E1105.0.1.50", {"start": v(14.93, -62.2) * mm, "end": v(14.93, -62.83) * mm});
            skLineSegment(sketch, "E1105.0.1.51", {"start": v(14.93, -66.67) * mm, "end": v(14.93, -67.3) * mm});
            skLineSegment(sketch, "E1105.0.1.52", {"start": v(14.93, -57.74) * mm, "end": v(14.93, -58.36) * mm});
            skLineSegment(sketch, "E1105.0.2.0", {"start": v(14.93, -94.06) * mm, "end": v(16.37, -94.55) * mm});
            skLineSegment(sketch, "E1105.0.2.1", {"start": v(16.37, -81.15) * mm, "end": v(16.37, -81.78) * mm});
            skLineSegment(sketch, "E1105.0.2.2", {"start": v(14.93, -103) * mm, "end": v(16.37, -103.5) * mm});
            skLineSegment(sketch, "E1105.0.2.3", {"start": v(14.93, -76.19) * mm, "end": v(16.37, -76.68) * mm});
            skLineSegment(sketch, "E1105.0.2.4", {"start": v(14.93, -100.77) * mm, "end": v(16.37, -101.26) * mm});
            skLineSegment(sketch, "E1105.0.2.5", {"start": v(14.93, -82.9) * mm, "end": v(16.37, -83.38) * mm});
            skLineSegment(sketch, "E1105.0.2.6", {"start": v(14.93, -93.44) * mm, "end": v(14.93, -94.06) * mm});
            skLineSegment(sketch, "E1105.0.2.7", {"start": v(14.93, -102.38) * mm, "end": v(14.93, -103) * mm});
            skLineSegment(sketch, "E1105.0.2.8", {"start": v(16.37, -75.07) * mm, "end": v(14.93, -75.56) * mm});
            skLineSegment(sketch, "E1105.0.2.9", {"start": v(14.93, -87.36) * mm, "end": v(16.37, -87.85) * mm});
            skLineSegment(sketch, "E1105.0.2.10", {"start": v(14.93, -88.97) * mm, "end": v(14.93, -89.6) * mm});
            skLineSegment(sketch, "E1105.0.2.11", {"start": v(16.37, -92.95) * mm, "end": v(14.93, -93.44) * mm});
            skLineSegment(sketch, "E1105.0.2.12", {"start": v(16.37, -84.01) * mm, "end": v(14.93, -84.5) * mm});
            skLineSegment(sketch, "E1105.0.2.13", {"start": v(16.37, -101.89) * mm, "end": v(14.93, -102.38) * mm});
            skLineSegment(sketch, "E1105.0.2.14", {"start": v(14.93, -100.14) * mm, "end": v(14.93, -100.77) * mm});
            skLineSegment(sketch, "E1105.0.2.15", {"start": v(16.37, -95.18) * mm, "end": v(14.93, -95.67) * mm});
            skLineSegment(sketch, "E1105.0.2.16", {"start": v(14.93, -82.27) * mm, "end": v(14.93, -82.9) * mm});
            skLineSegment(sketch, "E1105.0.2.19", {"start": v(16.37, -88.48) * mm, "end": v(14.93, -88.97) * mm});
            skLineSegment(sketch, "E1105.0.2.20", {"start": v(16.37, -101.26) * mm, "end": v(16.37, -101.89) * mm});
            skLineSegment(sketch, "E1105.0.2.21", {"start": v(14.93, -89.6) * mm, "end": v(16.37, -90.09) * mm});
            skLineSegment(sketch, "E1105.0.2.22", {"start": v(16.37, -87.85) * mm, "end": v(16.37, -88.48) * mm});
            skLineSegment(sketch, "E1105.0.2.23", {"start": v(14.93, -80.66) * mm, "end": v(16.37, -81.15) * mm});
            skLineSegment(sketch, "E1105.0.2.24", {"start": v(14.93, -75.56) * mm, "end": v(14.93, -76.19) * mm});
            skLineSegment(sketch, "E1105.0.2.25", {"start": v(16.37, -99.65) * mm, "end": v(14.93, -100.14) * mm});
            skLineSegment(sketch, "E1105.0.2.26", {"start": v(16.37, -90.71) * mm, "end": v(14.93, -91.2) * mm});
            skLineSegment(sketch, "E1105.0.2.27", {"start": v(16.37, -94.55) * mm, "end": v(16.37, -95.18) * mm});
            skLineSegment(sketch, "E1105.0.2.28", {"start": v(16.37, -81.78) * mm, "end": v(14.93, -82.27) * mm});
            skLineSegment(sketch, "E1105.0.2.30", {"start": v(16.37, -99.02) * mm, "end": v(16.37, -99.65) * mm});
            skLineSegment(sketch, "E1105.0.2.31", {"start": v(16.37, -90.09) * mm, "end": v(16.37, -90.71) * mm});
            skLineSegment(sketch, "E1105.0.2.32", {"start": v(14.93, -85.13) * mm, "end": v(16.37, -85.62) * mm});
            skLineSegment(sketch, "E1105.0.2.33", {"start": v(14.93, -91.83) * mm, "end": v(16.37, -92.32) * mm});
            skLineSegment(sketch, "E1105.0.2.34", {"start": v(16.37, -96.79) * mm, "end": v(16.37, -97.42) * mm});
            skLineSegment(sketch, "E1105.0.2.35", {"start": v(14.93, -84.5) * mm, "end": v(14.93, -85.13) * mm});
            skLineSegment(sketch, "E1105.0.2.36", {"start": v(16.37, -78.91) * mm, "end": v(16.37, -79.54) * mm});
            skLineSegment(sketch, "E1105.0.2.37", {"start": v(14.93, -96.3) * mm, "end": v(16.37, -96.79) * mm});
            skLineSegment(sketch, "E1105.0.2.38", {"start": v(14.93, -97.9) * mm, "end": v(14.93, -98.53) * mm});
            skLineSegment(sketch, "E1105.0.2.39", {"start": v(14.93, -78.42) * mm, "end": v(16.37, -78.91) * mm});
            skLineSegment(sketch, "E1105.0.2.40", {"start": v(14.93, -80.03) * mm, "end": v(14.93, -80.66) * mm});
            skLineSegment(sketch, "E1105.0.2.41", {"start": v(16.37, -86.25) * mm, "end": v(14.93, -86.74) * mm});
            skLineSegment(sketch, "E1105.0.2.42", {"start": v(16.37, -97.42) * mm, "end": v(14.93, -97.9) * mm});
            skLineSegment(sketch, "E1105.0.2.43", {"start": v(16.37, -92.32) * mm, "end": v(16.37, -92.95) * mm});
            skLineSegment(sketch, "E1105.0.2.44", {"start": v(16.37, -83.38) * mm, "end": v(16.37, -84.01) * mm});
            skLineSegment(sketch, "E1105.0.2.45", {"start": v(16.37, -79.54) * mm, "end": v(14.93, -80.03) * mm});
            skLineSegment(sketch, "E1105.0.2.46", {"start": v(14.93, -98.53) * mm, "end": v(16.37, -99.02) * mm});
            skLineSegment(sketch, "E1105.0.2.47", {"start": v(16.37, -85.62) * mm, "end": v(16.37, -86.25) * mm});
            skLineSegment(sketch, "E1105.0.2.48", {"start": v(14.93, -77.8) * mm, "end": v(14.93, -78.42) * mm});
            skLineSegment(sketch, "E1105.0.2.49", {"start": v(16.37, -76.68) * mm, "end": v(16.37, -77.3) * mm});
            skLineSegment(sketch, "E1105.0.2.50", {"start": v(14.93, -91.2) * mm, "end": v(14.93, -91.83) * mm});
            skLineSegment(sketch, "E1105.0.2.51", {"start": v(14.93, -95.67) * mm, "end": v(14.93, -96.3) * mm});
            skLineSegment(sketch, "E1105.0.2.52", {"start": v(14.93, -86.74) * mm, "end": v(14.93, -87.36) * mm});
            skLineSegment(sketch, "E1105.0.3.0", {"start": v(14.93, -123.06) * mm, "end": v(16.37, -123.55) * mm});
            skLineSegment(sketch, "E1105.0.3.1", {"start": v(16.37, -110.15) * mm, "end": v(16.37, -110.78) * mm});
            skLineSegment(sketch, "E1105.0.3.2", {"start": v(14.93, -132) * mm, "end": v(16.37, -132.5) * mm});
            skLineSegment(sketch, "E1105.0.3.3", {"start": v(14.93, -105.19) * mm, "end": v(16.37, -105.68) * mm});
            skLineSegment(sketch, "E1105.0.3.4", {"start": v(14.93, -129.77) * mm, "end": v(16.37, -130.26) * mm});
            skLineSegment(sketch, "E1105.0.3.5", {"start": v(14.93, -111.9) * mm, "end": v(16.37, -112.38) * mm});
            skLineSegment(sketch, "E1105.0.3.6", {"start": v(14.93, -122.44) * mm, "end": v(14.93, -123.06) * mm});
            skLineSegment(sketch, "E1105.0.3.7", {"start": v(14.93, -131.38) * mm, "end": v(14.93, -132) * mm});
            skLineSegment(sketch, "E1105.0.3.8", {"start": v(16.37, -104.07) * mm, "end": v(14.93, -104.56) * mm});
            skLineSegment(sketch, "E1105.0.3.9", {"start": v(14.93, -116.36) * mm, "end": v(16.37, -116.85) * mm});
            skLineSegment(sketch, "E1105.0.3.10", {"start": v(14.93, -117.97) * mm, "end": v(14.93, -118.6) * mm});
            skLineSegment(sketch, "E1105.0.3.11", {"start": v(16.37, -121.95) * mm, "end": v(14.93, -122.44) * mm});
            skLineSegment(sketch, "E1105.0.3.12", {"start": v(16.37, -113.01) * mm, "end": v(14.93, -113.5) * mm});
            skLineSegment(sketch, "E1105.0.3.13", {"start": v(16.37, -130.89) * mm, "end": v(14.93, -131.38) * mm});
            skLineSegment(sketch, "E1105.0.3.14", {"start": v(14.93, -129.14) * mm, "end": v(14.93, -129.77) * mm});
            skLineSegment(sketch, "E1105.0.3.15", {"start": v(16.37, -124.18) * mm, "end": v(14.93, -124.67) * mm});
            skLineSegment(sketch, "E1105.0.3.16", {"start": v(14.93, -111.27) * mm, "end": v(14.93, -111.9) * mm});
            skLineSegment(sketch, "E1105.0.3.17", {"start": v(16.37, -132.8) * mm, "end": v(17.87, -132.8) * mm});
            skLineSegment(sketch, "E1105.0.3.18", {"start": v(16.37, -106.3) * mm, "end": v(14.93, -106.8) * mm});
            skLineSegment(sketch, "E1105.0.3.19", {"start": v(16.37, -117.48) * mm, "end": v(14.93, -117.97) * mm});
            skLineSegment(sketch, "E1105.0.3.20", {"start": v(16.37, -130.26) * mm, "end": v(16.37, -130.89) * mm});
            skLineSegment(sketch, "E1105.0.3.21", {"start": v(14.93, -118.6) * mm, "end": v(16.37, -119.09) * mm});
            skLineSegment(sketch, "E1105.0.3.22", {"start": v(16.37, -116.85) * mm, "end": v(16.37, -117.48) * mm});
            skLineSegment(sketch, "E1105.0.3.23", {"start": v(14.93, -109.66) * mm, "end": v(16.37, -110.15) * mm});
            skLineSegment(sketch, "E1105.0.3.24", {"start": v(14.93, -104.56) * mm, "end": v(14.93, -105.19) * mm});
            skLineSegment(sketch, "E1105.0.3.25", {"start": v(16.37, -128.65) * mm, "end": v(14.93, -129.14) * mm});
            skLineSegment(sketch, "E1105.0.3.26", {"start": v(16.37, -119.71) * mm, "end": v(14.93, -120.2) * mm});
            skLineSegment(sketch, "E1105.0.3.27", {"start": v(16.37, -123.55) * mm, "end": v(16.37, -124.18) * mm});
            skLineSegment(sketch, "E1105.0.3.28", {"start": v(16.37, -110.78) * mm, "end": v(14.93, -111.27) * mm});
            skLineSegment(sketch, "E1105.0.3.29", {"start": v(16.37, -132.5) * mm, "end": v(16.37, -132.8) * mm});
            skLineSegment(sketch, "E1105.0.3.30", {"start": v(16.37, -128.02) * mm, "end": v(16.37, -128.65) * mm});
            skLineSegment(sketch, "E1105.0.3.31", {"start": v(16.37, -119.09) * mm, "end": v(16.37, -119.71) * mm});
            skLineSegment(sketch, "E1105.0.3.32", {"start": v(14.93, -114.13) * mm, "end": v(16.37, -114.62) * mm});
            skLineSegment(sketch, "E1105.0.3.33", {"start": v(14.93, -120.83) * mm, "end": v(16.37, -121.32) * mm});
            skLineSegment(sketch, "E1105.0.3.34", {"start": v(16.37, -125.79) * mm, "end": v(16.37, -126.42) * mm});
            skLineSegment(sketch, "E1105.0.3.35", {"start": v(14.93, -113.5) * mm, "end": v(14.93, -114.13) * mm});
            skLineSegment(sketch, "E1105.0.3.36", {"start": v(16.37, -107.91) * mm, "end": v(16.37, -108.54) * mm});
            skLineSegment(sketch, "E1105.0.3.37", {"start": v(14.93, -125.3) * mm, "end": v(16.37, -125.79) * mm});
            skLineSegment(sketch, "E1105.0.3.38", {"start": v(14.93, -126.9) * mm, "end": v(14.93, -127.53) * mm});
            skLineSegment(sketch, "E1105.0.3.39", {"start": v(14.93, -107.42) * mm, "end": v(16.37, -107.91) * mm});
            skLineSegment(sketch, "E1105.0.3.40", {"start": v(14.93, -109.03) * mm, "end": v(14.93, -109.66) * mm});
            skLineSegment(sketch, "E1105.0.3.41", {"start": v(16.37, -115.25) * mm, "end": v(14.93, -115.74) * mm});
            skLineSegment(sketch, "E1105.0.3.42", {"start": v(16.37, -126.42) * mm, "end": v(14.93, -126.9) * mm});
            skLineSegment(sketch, "E1105.0.3.43", {"start": v(16.37, -121.32) * mm, "end": v(16.37, -121.95) * mm});
            skLineSegment(sketch, "E1105.0.3.44", {"start": v(16.37, -112.38) * mm, "end": v(16.37, -113.01) * mm});
            skLineSegment(sketch, "E1105.0.3.45", {"start": v(16.37, -108.54) * mm, "end": v(14.93, -109.03) * mm});
            skLineSegment(sketch, "E1105.0.3.46", {"start": v(14.93, -127.53) * mm, "end": v(16.37, -128.02) * mm});
            skLineSegment(sketch, "E1105.0.3.47", {"start": v(16.37, -114.62) * mm, "end": v(16.37, -115.25) * mm});
            skLineSegment(sketch, "E1105.0.3.48", {"start": v(14.93, -106.8) * mm, "end": v(14.93, -107.42) * mm});
            skLineSegment(sketch, "E1105.0.3.49", {"start": v(16.37, -105.68) * mm, "end": v(16.37, -106.3) * mm});
            skLineSegment(sketch, "E1105.0.3.50", {"start": v(14.93, -120.2) * mm, "end": v(14.93, -120.83) * mm});
            skLineSegment(sketch, "E1105.0.3.51", {"start": v(14.93, -124.67) * mm, "end": v(14.93, -125.3) * mm});
            skLineSegment(sketch, "E1105.0.3.52", {"start": v(14.93, -115.74) * mm, "end": v(14.93, -116.36) * mm});
            skLineSegment(sketch, "E1105.direction1", {"start": v(14.93, -36.06) * mm, "end": v(39.93, -36.06) * mm, "construction": true});
            skLineSegment(sketch, "E1105.direction2", {"start": v(14.93, -36.06) * mm, "end": v(14.93, -65.06) * mm, "construction": true});
            skLineSegment(sketch, "E1106", {"start": v(16.37, -74.5) * mm, "end": v(16.37, -75.07) * mm});
            skLineSegment(sketch, "E1107", {"start": v(16.37, -104.07) * mm, "end": v(16.37, -103.5) * mm});
            skLineSegment(sketch, "E1108", {"start": v(14.93, -77.8) * mm, "end": v(16.37, -77.3) * mm});
            skLineSegment(sketch, "E1109", {"start": v(17.87, -132.8) * mm, "end": v(17.87, -45.8) * mm});
            skLineSegment(sketch, "E1110", {"start": v(16.37, -45.5) * mm, "end": v(16.37, -46.07) * mm});
            skSolve(sketch);
        }
        {
            var Q0;
            Q0=makeQuery(id+"F0.imprint","IMPRINT",FACE,{"disambiguationData":[TD([[makeQuery(id+"F0.imprint","IMPRINT",EDGE,{"derivedFrom":sQuery(id+"F0.wireOp",EDGE,"E936")}),1.0]])]});
            var Q1;
            Q1=makeQuery(id+"F0.imprint","IMPRINT",FACE,{"disambiguationData":[TD([[makeQuery(id+"F0.imprint","IMPRINT",EDGE,{"derivedFrom":sQuery(id+"F0.wireOp",EDGE,"E0")}),1.0]])]});
            extrude(context, id + "F1", {"entities" : qUnion([Q0, Q1]), "depth" : 6 * mm});
        }
    });
